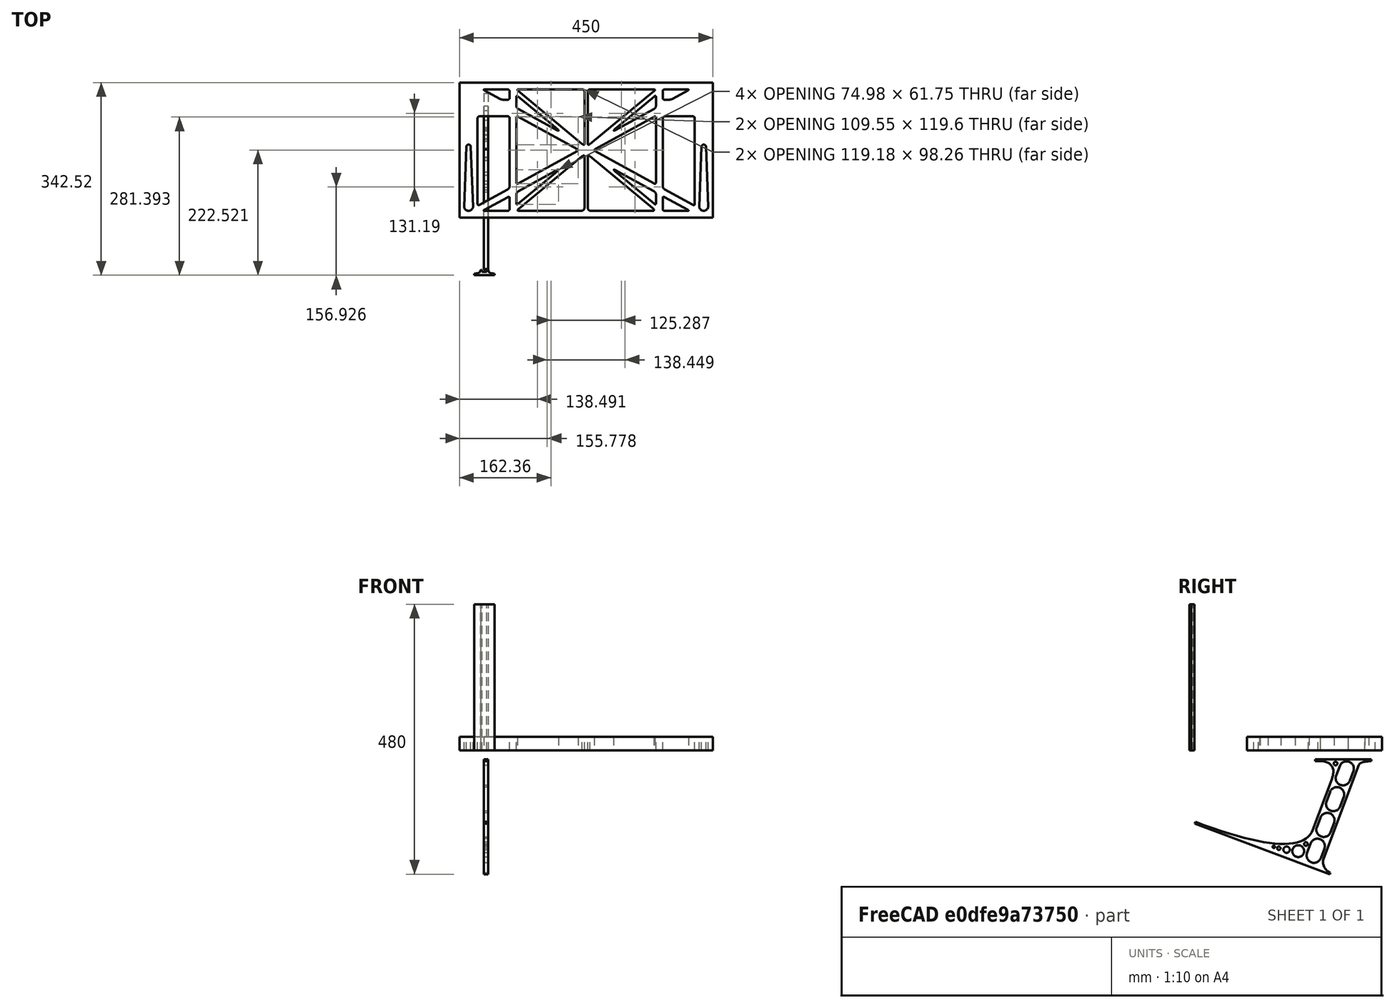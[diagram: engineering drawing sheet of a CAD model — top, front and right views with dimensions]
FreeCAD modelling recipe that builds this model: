
FCSTD DOCUMENT  (FreeCAD 0.19R0.19.2)
Label: laptopStand150FCStd
License: All rights reserved
LicenseURL: http://en.wikipedia.org/wiki/All_rights_reserved
objects: Sketcher::SketchObject×4, Part::Extrusion×3
note: 7 computed .brp shape members not serialized (recipe doc carries the construction recipe); baked Part::Feature solids carry a one-line shape summary decoded from their .brp

FEATURE [Sketcher::SketchObject] Sketch
  FullyConstrained = false
  sketch-geometry (349):
    g0: LineSegment StartX=-10.9272 StartY=-82.7794 StartZ=0 EndX=46.0728 EndY=-51.4823 EndZ=0
    g1: LineSegment StartX=-10.9272 StartY=76.4095 StartZ=0 EndX=-10.9272 EndY=-82.7794 EndZ=0
    g2: LineSegment StartX=46.0728 StartY=76.4095 StartZ=0 EndX=46.0728 EndY=-51.4823 EndZ=0
    g3: LineSegment StartX=-42.9272 StartY=136.221 StartZ=0 EndX=-42.9272 EndY=-103.779 EndZ=0
    g4: LineSegment StartX=407.073 StartY=136.221 StartZ=0 EndX=407.073 EndY=-103.779 EndZ=0
    g5: ArcOfCircle CenterX=-26.9272 CenterY=-83.7794 CenterZ=0 NormalX=0 NormalY=0 NormalZ=1 AngleXU=0 Radius=8 StartAngle=3.14159 EndAngle=6.28319
    g6: ArcOfCircle CenterX=391.073 CenterY=22.1087 CenterZ=0 NormalX=0 NormalY=0 NormalZ=1 AngleXU=0 Radius=8 StartAngle=-4.4e-15 EndAngle=3.14159
    g7: LineSegment StartX=399.073 StartY=22.1087 StartZ=0 EndX=399.073 EndY=-83.7794 EndZ=0
    g8: LineSegment StartX=383.073 StartY=22.1087 StartZ=0 EndX=383.073 EndY=-83.7794 EndZ=0
    g9: ArcOfCircle CenterX=391.073 CenterY=-83.7794 CenterZ=0 NormalX=0 NormalY=0 NormalZ=1 AngleXU=0 Radius=8 StartAngle=3.14159 EndAngle=6.28319
    g10: Circle CenterX=175.022 CenterY=27.0628 CenterZ=0 NormalX=0 NormalY=0 NormalZ=1 AngleXU=0 Radius=1
    g11: Circle CenterX=179.022 CenterY=24.8665 CenterZ=0 NormalX=0 NormalY=0 NormalZ=1 AngleXU=0 Radius=1
    g12: Circle CenterX=179.022 CenterY=27.0628 CenterZ=0 NormalX=0 NormalY=0 NormalZ=1 AngleXU=0 Radius=1
    g13: BSplineCurve PolesCount=3 KnotsCount=2 Degree=2 IsPeriodic=0
    g14: GeomPoint X=175.022 Y=27.0628 Z=0
    g15: GeomPoint X=179.022 Y=27.0628 Z=0
    g16: Circle CenterX=189.124 CenterY=27.0628 CenterZ=0 NormalX=0 NormalY=0 NormalZ=1 AngleXU=0 Radius=1
    g17: Circle CenterX=185.124 CenterY=24.8665 CenterZ=0 NormalX=0 NormalY=0 NormalZ=1 AngleXU=0 Radius=1
    g18: Circle CenterX=185.124 CenterY=27.0628 CenterZ=0 NormalX=0 NormalY=0 NormalZ=1 AngleXU=0 Radius=1
    g19: BSplineCurve PolesCount=3 KnotsCount=2 Degree=2 IsPeriodic=0
    g20: GeomPoint X=189.124 Y=27.0628 Z=0
    g21: GeomPoint X=185.124 Y=27.0628 Z=0
    g22: Circle CenterX=175.022 CenterY=5.37834 CenterZ=0 NormalX=0 NormalY=0 NormalZ=1 AngleXU=0 Radius=1
    g23: Circle CenterX=179.022 CenterY=7.57463 CenterZ=0 NormalX=0 NormalY=0 NormalZ=1 AngleXU=0 Radius=1
    g24: Circle CenterX=179.022 CenterY=5.34704 CenterZ=0 NormalX=0 NormalY=0 NormalZ=1 AngleXU=0 Radius=1
    g25: BSplineCurve PolesCount=3 KnotsCount=2 Degree=2 IsPeriodic=0
    g26: GeomPoint X=175.022 Y=5.37834 Z=0
    g27: GeomPoint X=179.022 Y=5.34704 Z=0
    g28: Circle CenterX=189.124 CenterY=5.37834 CenterZ=0 NormalX=0 NormalY=0 NormalZ=1 AngleXU=0 Radius=1
    g29: Circle CenterX=185.124 CenterY=7.57463 CenterZ=0 NormalX=0 NormalY=0 NormalZ=1 AngleXU=0 Radius=1
    g30: Circle CenterX=185.124 CenterY=5.34704 CenterZ=0 NormalX=0 NormalY=0 NormalZ=1 AngleXU=0 Radius=1
    g31: BSplineCurve PolesCount=3 KnotsCount=2 Degree=2 IsPeriodic=0
    g32: GeomPoint X=189.124 Y=5.37834 Z=0
    g33: GeomPoint X=185.124 Y=5.34704 Z=0
    g34: Circle CenterX=165.871 CenterY=18.1458 CenterZ=0 NormalX=0 NormalY=0 NormalZ=1 AngleXU=0 Radius=1
    g35: Circle CenterX=169.377 CenterY=16.2206 CenterZ=0 NormalX=0 NormalY=0 NormalZ=1 AngleXU=0 Radius=1
    g36: Circle CenterX=165.871 CenterY=14.2954 CenterZ=0 NormalX=0 NormalY=0 NormalZ=1 AngleXU=0 Radius=1
    g37: BSplineCurve PolesCount=3 KnotsCount=2 Degree=2 IsPeriodic=0
    g38: GeomPoint X=165.871 Y=18.1458 Z=0
    g39: GeomPoint X=165.871 Y=14.2954 Z=0
    g40: Circle CenterX=198.275 CenterY=18.1458 CenterZ=0 NormalX=0 NormalY=0 NormalZ=1 AngleXU=0 Radius=1
    g41: Circle CenterX=194.768 CenterY=16.2206 CenterZ=0 NormalX=0 NormalY=0 NormalZ=1 AngleXU=0 Radius=1
    g42: Circle CenterX=198.275 CenterY=14.2954 CenterZ=0 NormalX=0 NormalY=0 NormalZ=1 AngleXU=0 Radius=1
    g43: BSplineCurve PolesCount=3 KnotsCount=2 Degree=2 IsPeriodic=0
    g44: GeomPoint X=198.275 Y=18.1458 Z=0
    g45: GeomPoint X=198.275 Y=14.2954 Z=0
    g46: LineSegment StartX=407.073 StartY=-103.779 StartZ=0 EndX=-42.9272 EndY=-103.779 EndZ=0
    g47: LineSegment StartX=407.073 StartY=136.221 StartZ=0 EndX=-42.9272 EndY=136.221 EndZ=0
    g48: LineSegment StartX=46.0728 StartY=76.4095 StartZ=0 EndX=-10.9272 EndY=76.4095 EndZ=0
    g49: Circle CenterX=125.607 CenterY=54.1951 CenterZ=0 NormalX=0 NormalY=0 NormalZ=1 AngleXU=0 Radius=1
    g50: Circle CenterX=139.632 CenterY=46.4944 CenterZ=0 NormalX=0 NormalY=0 NormalZ=1 AngleXU=0 Radius=1
    g51: Circle CenterX=127.326 CenterY=56.7187 CenterZ=0 NormalX=0 NormalY=0 NormalZ=1 AngleXU=0 Radius=1
    g52: BSplineCurve PolesCount=3 KnotsCount=2 Degree=2 IsPeriodic=0
    g53: GeomPoint X=125.607 Y=54.1951 Z=0
    g54: GeomPoint X=127.326 Y=56.7187 Z=0
    g55: Circle CenterX=236.821 CenterY=56.7187 CenterZ=0 NormalX=0 NormalY=0 NormalZ=1 AngleXU=0 Radius=1
    g56: Circle CenterX=224.513 CenterY=46.4944 CenterZ=0 NormalX=0 NormalY=0 NormalZ=1 AngleXU=0 Radius=1
    g57: Circle CenterX=238.538 CenterY=54.1951 CenterZ=0 NormalX=0 NormalY=0 NormalZ=1 AngleXU=0 Radius=1
    g58: BSplineCurve PolesCount=3 KnotsCount=2 Degree=2 IsPeriodic=0
    g59: GeomPoint X=236.821 Y=56.7187 Z=0
    g60: GeomPoint X=238.538 Y=54.1951 Z=0
    g61: Circle CenterX=238.538 CenterY=-21.7539 CenterZ=0 NormalX=0 NormalY=0 NormalZ=1 AngleXU=0 Radius=1
    g62: Circle CenterX=224.513 CenterY=-14.0532 CenterZ=0 NormalX=0 NormalY=0 NormalZ=1 AngleXU=0 Radius=1
    g63: Circle CenterX=236.821 CenterY=-24.2775 CenterZ=0 NormalX=0 NormalY=0 NormalZ=1 AngleXU=0 Radius=1
    g64: BSplineCurve PolesCount=3 KnotsCount=2 Degree=2 IsPeriodic=0
    g65: GeomPoint X=238.538 Y=-21.7539 Z=0
    g66: GeomPoint X=236.821 Y=-24.2775 Z=0
    g67: Circle CenterX=125.607 CenterY=-21.7539 CenterZ=0 NormalX=0 NormalY=0 NormalZ=1 AngleXU=0 Radius=1
    g68: Circle CenterX=139.632 CenterY=-14.0532 CenterZ=0 NormalX=0 NormalY=0 NormalZ=1 AngleXU=0 Radius=1
    g69: Circle CenterX=127.325 CenterY=-24.2775 CenterZ=0 NormalX=0 NormalY=0 NormalZ=1 AngleXU=0 Radius=1
    g70: BSplineCurve PolesCount=3 KnotsCount=2 Degree=2 IsPeriodic=0
    g71: GeomPoint X=125.607 Y=-21.7539 Z=0
    g72: GeomPoint X=127.325 Y=-24.2775 Z=0
    g73: Circle CenterX=302.996 CenterY=111.695 CenterZ=0 NormalX=0 NormalY=0 NormalZ=1 AngleXU=0 Radius=1
    g74: Circle CenterX=306.073 CenterY=114.251 CenterZ=0 NormalX=0 NormalY=0 NormalZ=1 AngleXU=0 Radius=1
    g75: Circle CenterX=306.073 CenterY=110.251 CenterZ=0 NormalX=0 NormalY=0 NormalZ=1 AngleXU=0 Radius=1
    g76: BSplineCurve PolesCount=3 KnotsCount=2 Degree=2 IsPeriodic=0
    g77: GeomPoint X=302.996 Y=111.695 Z=0
    g78: GeomPoint X=306.073 Y=110.251 Z=0
    g79: Circle CenterX=306.073 CenterY=95.2763 CenterZ=0 NormalX=0 NormalY=0 NormalZ=1 AngleXU=0 Radius=1
    g80: Circle CenterX=306.073 CenterY=91.2763 CenterZ=0 NormalX=0 NormalY=0 NormalZ=1 AngleXU=0 Radius=1
    g81: Circle CenterX=302.567 CenterY=89.3511 CenterZ=0 NormalX=0 NormalY=0 NormalZ=1 AngleXU=0 Radius=1
    g82: BSplineCurve PolesCount=3 KnotsCount=2 Degree=2 IsPeriodic=0
    g83: GeomPoint X=306.073 Y=95.2763 Z=0
    g84: GeomPoint X=302.567 Y=89.3511 Z=0
    g85: LineSegment StartX=306.073 StartY=110.251 StartZ=0 EndX=306.073 EndY=95.2763 EndZ=0
    g86: LineSegment StartX=302.996 StartY=111.695 StartZ=0 EndX=236.821 EndY=56.7187 EndZ=0
    g87: LineSegment StartX=238.538 StartY=54.1951 StartZ=0 EndX=302.567 EndY=89.3511 EndZ=0
    g88: Circle CenterX=61.1496 CenterY=111.695 CenterZ=0 NormalX=0 NormalY=0 NormalZ=1 AngleXU=0 Radius=1
    g89: Circle CenterX=58.0728 CenterY=114.251 CenterZ=0 NormalX=0 NormalY=0 NormalZ=1 AngleXU=0 Radius=1
    g90: Circle CenterX=58.0728 CenterY=110.251 CenterZ=0 NormalX=0 NormalY=0 NormalZ=1 AngleXU=0 Radius=1
    g91: BSplineCurve PolesCount=3 KnotsCount=2 Degree=2 IsPeriodic=0
    g92: GeomPoint X=61.1496 Y=111.695 Z=0
    g93: GeomPoint X=58.0728 Y=110.251 Z=0
    g94: Circle CenterX=61.5791 CenterY=89.3511 CenterZ=0 NormalX=0 NormalY=0 NormalZ=1 AngleXU=0 Radius=1
    g95: Circle CenterX=58.0728 CenterY=91.2763 CenterZ=0 NormalX=0 NormalY=0 NormalZ=1 AngleXU=0 Radius=1
    g96: Circle CenterX=58.0728 CenterY=95.2763 CenterZ=0 NormalX=0 NormalY=0 NormalZ=1 AngleXU=0 Radius=1
    g97: BSplineCurve PolesCount=3 KnotsCount=2 Degree=2 IsPeriodic=0
    g98: GeomPoint X=61.5791 Y=89.3511 Z=0
    g99: GeomPoint X=58.0728 Y=95.2763 Z=0
    g100: LineSegment StartX=58.0728 StartY=110.251 StartZ=0 EndX=58.0728 EndY=95.2763 EndZ=0
    g101: LineSegment StartX=61.1496 StartY=111.695 StartZ=0 EndX=127.326 EndY=56.7187 EndZ=0
    g102: LineSegment StartX=125.607 StartY=54.1951 StartZ=0 EndX=61.5791 EndY=89.3511 EndZ=0
    g103: Circle CenterX=61.5791 CenterY=-56.9099 CenterZ=0 NormalX=0 NormalY=0 NormalZ=1 AngleXU=0 Radius=1
    g104: Circle CenterX=58.0728 CenterY=-58.8351 CenterZ=0 NormalX=0 NormalY=0 NormalZ=1 AngleXU=0 Radius=1
    g105: Circle CenterX=58.0728 CenterY=-62.8351 CenterZ=0 NormalX=0 NormalY=0 NormalZ=1 AngleXU=0 Radius=1
    g106: BSplineCurve PolesCount=3 KnotsCount=2 Degree=2 IsPeriodic=0
    g107: GeomPoint X=61.5791 Y=-56.9099 Z=0
    g108: GeomPoint X=58.0728 Y=-62.8351 Z=0
    g109: Circle CenterX=58.0728 CenterY=-77.8102 CenterZ=0 NormalX=0 NormalY=0 NormalZ=1 AngleXU=0 Radius=1
    g110: Circle CenterX=58.0728 CenterY=-81.8102 CenterZ=0 NormalX=0 NormalY=0 NormalZ=1 AngleXU=0 Radius=1
    g111: Circle CenterX=61.1496 CenterY=-79.2541 CenterZ=0 NormalX=0 NormalY=0 NormalZ=1 AngleXU=0 Radius=1
    g112: BSplineCurve PolesCount=3 KnotsCount=2 Degree=2 IsPeriodic=0
    g113: GeomPoint X=58.0728 Y=-77.8102 Z=0
    g114: GeomPoint X=61.1496 Y=-79.2541 Z=0
    g115: LineSegment StartX=58.0728 StartY=-62.8351 StartZ=0 EndX=58.0728 EndY=-77.8102 EndZ=0
    g116: LineSegment StartX=61.1496 StartY=-79.2541 StartZ=0 EndX=127.325 EndY=-24.2775 EndZ=0
    g117: LineSegment StartX=125.607 StartY=-21.7539 StartZ=0 EndX=61.5791 EndY=-56.9099 EndZ=0
    g118: Circle CenterX=302.567 CenterY=-56.9099 CenterZ=0 NormalX=0 NormalY=0 NormalZ=1 AngleXU=0 Radius=1
    g119: Circle CenterX=306.073 CenterY=-58.8351 CenterZ=0 NormalX=0 NormalY=0 NormalZ=1 AngleXU=0 Radius=1
    g120: Circle CenterX=306.073 CenterY=-62.8351 CenterZ=0 NormalX=0 NormalY=0 NormalZ=1 AngleXU=0 Radius=1
    g121: BSplineCurve PolesCount=3 KnotsCount=2 Degree=2 IsPeriodic=0
    g122: GeomPoint X=302.567 Y=-56.9099 Z=0
    g123: GeomPoint X=306.073 Y=-62.8351 Z=0
    g124: Circle CenterX=302.996 CenterY=-79.2541 CenterZ=0 NormalX=0 NormalY=0 NormalZ=1 AngleXU=0 Radius=1
    g125: Circle CenterX=306.073 CenterY=-81.8102 CenterZ=0 NormalX=0 NormalY=0 NormalZ=1 AngleXU=0 Radius=1
    g126: Circle CenterX=306.073 CenterY=-77.8102 CenterZ=0 NormalX=0 NormalY=0 NormalZ=1 AngleXU=0 Radius=1
    g127: BSplineCurve PolesCount=3 KnotsCount=2 Degree=2 IsPeriodic=0
    g128: GeomPoint X=302.996 Y=-79.2541 Z=0
    g129: GeomPoint X=306.073 Y=-77.8102 Z=0
    g130: LineSegment StartX=306.073 StartY=-62.8351 StartZ=0 EndX=306.073 EndY=-77.8102 EndZ=0
    g131: LineSegment StartX=302.996 StartY=-79.2541 StartZ=0 EndX=236.821 EndY=-24.2775 EndZ=0
    g132: LineSegment StartX=238.538 StartY=-21.7539 StartZ=0 EndX=302.567 EndY=-56.9099 EndZ=0
    g133: Circle CenterX=61.6457 CenterY=-88.8112 CenterZ=0 NormalX=0 NormalY=0 NormalZ=1 AngleXU=0 Radius=1
    g134: Circle CenterX=58.0728 CenterY=-91.7794 CenterZ=0 NormalX=0 NormalY=0 NormalZ=1 AngleXU=0 Radius=1
    g135: Circle CenterX=63.9135 CenterY=-91.7794 CenterZ=0 NormalX=0 NormalY=0 NormalZ=1 AngleXU=0 Radius=1
    g136: BSplineCurve PolesCount=3 KnotsCount=2 Degree=2 IsPeriodic=0
    g137: GeomPoint X=61.6457 Y=-88.8112 Z=0
    g138: GeomPoint X=63.9135 Y=-91.7794 Z=0
    g139: Circle CenterX=179.022 CenterY=-85.8163 CenterZ=0 NormalX=0 NormalY=0 NormalZ=1 AngleXU=0 Radius=1
    g140: Circle CenterX=179.022 CenterY=-91.7794 CenterZ=0 NormalX=0 NormalY=0 NormalZ=1 AngleXU=0 Radius=1
    g141: Circle CenterX=171.895 CenterY=-91.7794 CenterZ=0 NormalX=0 NormalY=0 NormalZ=1 AngleXU=0 Radius=1
    g142: BSplineCurve PolesCount=3 KnotsCount=2 Degree=2 IsPeriodic=0
    g143: GeomPoint X=179.022 Y=-85.8163 Z=0
    g144: GeomPoint X=171.895 Y=-91.7794 Z=0
    g145: Circle CenterX=185.124 CenterY=-86.2028 CenterZ=0 NormalX=0 NormalY=0 NormalZ=1 AngleXU=0 Radius=1
    g146: Circle CenterX=185.124 CenterY=-91.7794 CenterZ=0 NormalX=0 NormalY=0 NormalZ=1 AngleXU=0 Radius=1
    g147: Circle CenterX=191.747 CenterY=-91.7794 CenterZ=0 NormalX=0 NormalY=0 NormalZ=1 AngleXU=0 Radius=1
    g148: BSplineCurve PolesCount=3 KnotsCount=2 Degree=2 IsPeriodic=0
    g149: GeomPoint X=185.124 Y=-86.2028 Z=0
    g150: GeomPoint X=191.747 Y=-91.7794 Z=0
    g151: Circle CenterX=299.888 CenterY=-86.6413 CenterZ=0 NormalX=0 NormalY=0 NormalZ=1 AngleXU=0 Radius=1
    g152: Circle CenterX=306.073 CenterY=-91.7794 CenterZ=0 NormalX=0 NormalY=0 NormalZ=1 AngleXU=0 Radius=1
    g153: Circle CenterX=298.776 CenterY=-91.7794 CenterZ=0 NormalX=0 NormalY=0 NormalZ=1 AngleXU=0 Radius=1
    g154: BSplineCurve PolesCount=3 KnotsCount=2 Degree=2 IsPeriodic=0
    g155: GeomPoint X=299.888 Y=-86.6413 Z=0
    g156: GeomPoint X=298.776 Y=-91.7794 Z=0
    g157: LineSegment StartX=189.124 StartY=5.37834 StartZ=0 EndX=299.888 EndY=-86.6413 EndZ=0
    g158: LineSegment StartX=298.776 StartY=-91.7794 StartZ=0 EndX=191.747 EndY=-91.7794 EndZ=0
    g159: LineSegment StartX=185.124 StartY=-86.2028 StartZ=0 EndX=185.124 EndY=5.34704 EndZ=0
    g160: LineSegment StartX=179.022 StartY=5.34704 StartZ=0 EndX=179.022 EndY=-85.8163 EndZ=0
    g161: LineSegment StartX=171.895 StartY=-91.7794 StartZ=0 EndX=63.9135 EndY=-91.7794 EndZ=0
    g162: LineSegment StartX=61.6457 StartY=-88.8112 StartZ=0 EndX=175.022 EndY=5.37834 EndZ=0
    g163: Circle CenterX=302.073 CenterY=124.221 CenterZ=0 NormalX=0 NormalY=0 NormalZ=1 AngleXU=0 Radius=1
    g164: Circle CenterX=306.073 CenterY=124.221 CenterZ=0 NormalX=0 NormalY=0 NormalZ=1 AngleXU=0 Radius=1
    g165: Circle CenterX=302.996 CenterY=121.665 CenterZ=0 NormalX=0 NormalY=0 NormalZ=1 AngleXU=0 Radius=1
    g166: BSplineCurve PolesCount=3 KnotsCount=2 Degree=2 IsPeriodic=0
    g167: GeomPoint X=302.073 Y=124.221 Z=0
    g168: GeomPoint X=302.996 Y=121.665 Z=0
    g169: Circle CenterX=189.124 CenterY=124.221 CenterZ=0 NormalX=0 NormalY=0 NormalZ=1 AngleXU=0 Radius=1
    g170: Circle CenterX=185.124 CenterY=124.221 CenterZ=0 NormalX=0 NormalY=0 NormalZ=1 AngleXU=0 Radius=1
    g171: Circle CenterX=185.124 CenterY=120.221 CenterZ=0 NormalX=0 NormalY=0 NormalZ=1 AngleXU=0 Radius=1
    g172: BSplineCurve PolesCount=3 KnotsCount=2 Degree=2 IsPeriodic=0
    g173: GeomPoint X=189.124 Y=124.221 Z=0
    g174: GeomPoint X=185.124 Y=120.221 Z=0
    g175: Circle CenterX=175.022 CenterY=124.221 CenterZ=0 NormalX=0 NormalY=0 NormalZ=1 AngleXU=0 Radius=1
    g176: Circle CenterX=179.022 CenterY=124.221 CenterZ=0 NormalX=0 NormalY=0 NormalZ=1 AngleXU=0 Radius=1
    g177: Circle CenterX=179.022 CenterY=120.221 CenterZ=0 NormalX=0 NormalY=0 NormalZ=1 AngleXU=0 Radius=1
    g178: BSplineCurve PolesCount=3 KnotsCount=2 Degree=2 IsPeriodic=0
    g179: GeomPoint X=175.022 Y=124.221 Z=0
    g180: GeomPoint X=179.022 Y=120.221 Z=0
    g181: Circle CenterX=62.0728 CenterY=124.221 CenterZ=0 NormalX=0 NormalY=0 NormalZ=1 AngleXU=0 Radius=1
    g182: Circle CenterX=58.0728 CenterY=124.221 CenterZ=0 NormalX=0 NormalY=0 NormalZ=1 AngleXU=0 Radius=1
    g183: Circle CenterX=61.1496 CenterY=121.665 CenterZ=0 NormalX=0 NormalY=0 NormalZ=1 AngleXU=0 Radius=1
    g184: BSplineCurve PolesCount=3 KnotsCount=2 Degree=2 IsPeriodic=0
    g185: GeomPoint X=62.0728 Y=124.221 Z=0
    g186: GeomPoint X=61.1496 Y=121.665 Z=0
    g187: LineSegment StartX=62.0728 StartY=124.221 StartZ=0 EndX=175.022 EndY=124.221 EndZ=0
    g188: LineSegment StartX=179.022 StartY=120.221 StartZ=0 EndX=179.022 EndY=27.0628 EndZ=0
    g189: LineSegment StartX=185.124 StartY=27.0628 StartZ=0 EndX=185.124 EndY=120.221 EndZ=0
    g190: LineSegment StartX=189.124 StartY=124.221 StartZ=0 EndX=302.073 EndY=124.221 EndZ=0
    g191: LineSegment StartX=302.996 StartY=121.665 StartZ=0 EndX=189.124 EndY=27.0628 EndZ=0
    g192: LineSegment StartX=175.022 StartY=27.0628 StartZ=0 EndX=61.1496 EndY=121.665 EndZ=0
    g193: Circle CenterX=61.5791 CenterY=75.4095 CenterZ=0 NormalX=0 NormalY=0 NormalZ=1 AngleXU=0 Radius=1
    g194: Circle CenterX=58.0728 CenterY=77.3346 CenterZ=0 NormalX=0 NormalY=0 NormalZ=1 AngleXU=0 Radius=1
    g195: Circle CenterX=58.0728 CenterY=73.3346 CenterZ=0 NormalX=0 NormalY=0 NormalZ=1 AngleXU=0 Radius=1
    g196: BSplineCurve PolesCount=3 KnotsCount=2 Degree=2 IsPeriodic=0
    g197: GeomPoint X=61.5791 Y=75.4095 Z=0
    g198: GeomPoint X=58.0728 Y=73.3346 Z=0
    g199: Circle CenterX=58.0728 CenterY=-40.8935 CenterZ=0 NormalX=0 NormalY=0 NormalZ=1 AngleXU=0 Radius=1
    g200: Circle CenterX=58.0728 CenterY=-44.8935 CenterZ=0 NormalX=0 NormalY=0 NormalZ=1 AngleXU=0 Radius=1
    g201: Circle CenterX=61.5791 CenterY=-42.9683 CenterZ=0 NormalX=0 NormalY=0 NormalZ=1 AngleXU=0 Radius=1
    g202: BSplineCurve PolesCount=3 KnotsCount=2 Degree=2 IsPeriodic=0
    g203: GeomPoint X=58.0728 Y=-40.8935 Z=0
    g204: GeomPoint X=61.5791 Y=-42.9683 Z=0
    g205: LineSegment StartX=61.5791 StartY=-42.9683 StartZ=0 EndX=165.871 EndY=14.2954 EndZ=0
    g206: LineSegment StartX=165.871 StartY=18.1458 StartZ=0 EndX=61.5791 EndY=75.4095 EndZ=0
    g207: LineSegment StartX=58.0728 StartY=73.3346 StartZ=0 EndX=58.0728 EndY=-40.8935 EndZ=0
    g208: Circle CenterX=302.567 CenterY=-42.9683 CenterZ=0 NormalX=0 NormalY=0 NormalZ=1 AngleXU=0 Radius=1
    g209: Circle CenterX=306.073 CenterY=-44.8935 CenterZ=0 NormalX=0 NormalY=0 NormalZ=1 AngleXU=0 Radius=1
    g210: Circle CenterX=306.073 CenterY=-40.8935 CenterZ=0 NormalX=0 NormalY=0 NormalZ=1 AngleXU=0 Radius=1
    g211: BSplineCurve PolesCount=3 KnotsCount=2 Degree=2 IsPeriodic=0
    g212: GeomPoint X=302.567 Y=-42.9683 Z=0
    g213: GeomPoint X=306.073 Y=-40.8935 Z=0
    g214: Circle CenterX=306.073 CenterY=73.3346 CenterZ=0 NormalX=0 NormalY=0 NormalZ=1 AngleXU=0 Radius=1
    g215: Circle CenterX=306.073 CenterY=77.3346 CenterZ=0 NormalX=0 NormalY=0 NormalZ=1 AngleXU=0 Radius=1
    g216: Circle CenterX=302.567 CenterY=75.4095 CenterZ=0 NormalX=0 NormalY=0 NormalZ=1 AngleXU=0 Radius=1
    g217: BSplineCurve PolesCount=3 KnotsCount=2 Degree=2 IsPeriodic=0
    g218: GeomPoint X=306.073 Y=73.3346 Z=0
    g219: GeomPoint X=302.567 Y=75.4095 Z=0
    g220: LineSegment StartX=302.567 StartY=-42.9683 StartZ=0 EndX=198.275 EndY=14.2954 EndZ=0
    g221: LineSegment StartX=198.275 StartY=18.1458 StartZ=0 EndX=302.567 EndY=75.4095 EndZ=0
    g222: LineSegment StartX=306.073 StartY=73.3346 StartZ=0 EndX=306.073 EndY=-40.8935 EndZ=0
    g223: LineSegment StartX=322.073 StartY=105.865 StartZ=0 EndX=328.643 EndY=105.865 EndZ=0
    g224: LineSegment StartX=318.073 StartY=120.221 StartZ=0 EndX=318.073 EndY=109.865 EndZ=0
    g225: LineSegment StartX=336.157 StartY=107.779 StartZ=0 EndX=362.567 EndY=122.294 EndZ=0
    g226: Circle CenterX=362.073 CenterY=124.221 CenterZ=0 NormalX=0 NormalY=0 NormalZ=1 AngleXU=0 Radius=1
    g227: Circle CenterX=366.073 CenterY=124.221 CenterZ=0 NormalX=0 NormalY=0 NormalZ=1 AngleXU=0 Radius=1
    g228: Circle CenterX=362.567 CenterY=122.294 CenterZ=0 NormalX=0 NormalY=0 NormalZ=1 AngleXU=0 Radius=1
    g229: BSplineCurve PolesCount=3 KnotsCount=2 Degree=2 IsPeriodic=0
    g230: GeomPoint X=362.073 Y=124.221 Z=0
    g231: GeomPoint X=362.567 Y=122.294 Z=0
    g232: Circle CenterX=322.073 CenterY=124.221 CenterZ=0 NormalX=0 NormalY=0 NormalZ=1 AngleXU=0 Radius=1
    g233: Circle CenterX=318.073 CenterY=124.221 CenterZ=0 NormalX=0 NormalY=0 NormalZ=1 AngleXU=0 Radius=1
    g234: Circle CenterX=318.073 CenterY=120.221 CenterZ=0 NormalX=0 NormalY=0 NormalZ=1 AngleXU=0 Radius=1
    g235: BSplineCurve PolesCount=3 KnotsCount=2 Degree=2 IsPeriodic=0
    g236: GeomPoint X=322.073 Y=124.221 Z=0
    g237: GeomPoint X=318.073 Y=120.221 Z=0
    g238: Circle CenterX=322.073 CenterY=105.865 CenterZ=0 NormalX=0 NormalY=0 NormalZ=1 AngleXU=0 Radius=1
    g239: Circle CenterX=318.073 CenterY=105.865 CenterZ=0 NormalX=0 NormalY=0 NormalZ=1 AngleXU=0 Radius=1
    g240: Circle CenterX=318.073 CenterY=109.865 CenterZ=0 NormalX=0 NormalY=0 NormalZ=1 AngleXU=0 Radius=1
    g241: BSplineCurve PolesCount=3 KnotsCount=2 Degree=2 IsPeriodic=0
    g242: GeomPoint X=322.073 Y=105.865 Z=0
    g243: GeomPoint X=318.073 Y=109.865 Z=0
    g244: Circle CenterX=336.157 CenterY=107.779 CenterZ=0 NormalX=0 NormalY=0 NormalZ=1 AngleXU=0 Radius=1
    g245: Circle CenterX=332.651 CenterY=105.853 CenterZ=0 NormalX=0 NormalY=0 NormalZ=1 AngleXU=0 Radius=1
    g246: Circle CenterX=328.643 CenterY=105.865 CenterZ=0 NormalX=0 NormalY=0 NormalZ=1 AngleXU=0 Radius=1
    g247: BSplineCurve PolesCount=3 KnotsCount=2 Degree=2 IsPeriodic=0
    g248: GeomPoint X=336.157 Y=107.779 Z=0
    g249: GeomPoint X=328.643 Y=105.865 Z=0
    g250: LineSegment StartX=322.073 StartY=124.221 StartZ=0 EndX=362.073 EndY=124.221 EndZ=0
    g251: Circle CenterX=371.567 CenterY=-80.8644 CenterZ=0 NormalX=0 NormalY=0 NormalZ=1 AngleXU=0 Radius=1
    g252: Circle CenterX=375.073 CenterY=-82.7896 CenterZ=0 NormalX=0 NormalY=0 NormalZ=1 AngleXU=0 Radius=1
    g253: Circle CenterX=375.073 CenterY=-78.7896 CenterZ=0 NormalX=0 NormalY=0 NormalZ=1 AngleXU=0 Radius=1
    g254: BSplineCurve PolesCount=3 KnotsCount=2 Degree=2 IsPeriodic=0
    g255: GeomPoint X=371.567 Y=-80.8644 Z=0
    g256: GeomPoint X=375.073 Y=-78.7896 Z=0
    g257: Circle CenterX=321.579 CenterY=-53.4075 CenterZ=0 NormalX=0 NormalY=0 NormalZ=1 AngleXU=0 Radius=1
    g258: Circle CenterX=318.073 CenterY=-51.4823 CenterZ=0 NormalX=0 NormalY=0 NormalZ=1 AngleXU=0 Radius=1
    g259: Circle CenterX=318.073 CenterY=-47.4805 CenterZ=0 NormalX=0 NormalY=0 NormalZ=1 AngleXU=0 Radius=1
    g260: BSplineCurve PolesCount=3 KnotsCount=2 Degree=2 IsPeriodic=0
    g261: GeomPoint X=321.579 Y=-53.4075 Z=0
    g262: GeomPoint X=318.073 Y=-47.4805 Z=0
    g263: LineSegment StartX=371.567 StartY=-80.8644 StartZ=0 EndX=321.579 EndY=-53.4075 EndZ=0
    g264: Circle CenterX=321.579 CenterY=-67.3492 CenterZ=0 NormalX=0 NormalY=0 NormalZ=1 AngleXU=0 Radius=1
    g265: Circle CenterX=318.073 CenterY=-65.424 CenterZ=0 NormalX=0 NormalY=0 NormalZ=1 AngleXU=0 Radius=1
    g266: Circle CenterX=318.073 CenterY=-69.424 CenterZ=0 NormalX=0 NormalY=0 NormalZ=1 AngleXU=0 Radius=1
    g267: BSplineCurve PolesCount=3 KnotsCount=2 Degree=2 IsPeriodic=0
    g268: GeomPoint X=321.579 Y=-67.3492 Z=0
    g269: GeomPoint X=318.073 Y=-69.424 Z=0
    g270: Circle CenterX=362.567 CenterY=-89.8542 CenterZ=0 NormalX=0 NormalY=0 NormalZ=1 AngleXU=0 Radius=1
    g271: Circle CenterX=366.073 CenterY=-91.7794 CenterZ=0 NormalX=0 NormalY=0 NormalZ=1 AngleXU=0 Radius=1
    g272: Circle CenterX=362.073 CenterY=-91.7794 CenterZ=0 NormalX=0 NormalY=0 NormalZ=1 AngleXU=0 Radius=1
    g273: BSplineCurve PolesCount=3 KnotsCount=2 Degree=2 IsPeriodic=0
    g274: GeomPoint X=362.567 Y=-89.8542 Z=0
    g275: GeomPoint X=362.073 Y=-91.7794 Z=0
    g276: Circle CenterX=322.073 CenterY=-91.7794 CenterZ=0 NormalX=0 NormalY=0 NormalZ=1 AngleXU=0 Radius=1
    g277: Circle CenterX=318.073 CenterY=-91.7794 CenterZ=0 NormalX=0 NormalY=0 NormalZ=1 AngleXU=0 Radius=1
    g278: Circle CenterX=318.073 CenterY=-87.7794 CenterZ=0 NormalX=0 NormalY=0 NormalZ=1 AngleXU=0 Radius=1
    g279: BSplineCurve PolesCount=3 KnotsCount=2 Degree=2 IsPeriodic=0
    g280: GeomPoint X=322.073 Y=-91.7794 Z=0
    g281: GeomPoint X=318.073 Y=-87.7794 Z=0
    g282: LineSegment StartX=362.567 StartY=-89.8542 StartZ=0 EndX=321.579 EndY=-67.3492 EndZ=0
    g283: LineSegment StartX=318.073 StartY=-69.424 StartZ=0 EndX=318.073 EndY=-87.7794 EndZ=0
    g284: LineSegment StartX=322.073 StartY=-91.7794 StartZ=0 EndX=362.073 EndY=-91.7794 EndZ=0
    g285: Circle CenterX=2.07281 CenterY=124.221 CenterZ=0 NormalX=0 NormalY=0 NormalZ=1 AngleXU=0 Radius=1
    g286: Circle CenterX=1.57905 CenterY=122.295 CenterZ=0 NormalX=0 NormalY=0 NormalZ=1 AngleXU=0 Radius=1
    g287: BSplineCurve PolesCount=3 KnotsCount=2 Degree=2 IsPeriodic=0
    g288: GeomPoint X=2.07281 Y=124.221 Z=0
    g289: GeomPoint X=1.57905 Y=122.295 Z=0
    g290: Circle CenterX=42.0728 CenterY=124.221 CenterZ=0 NormalX=0 NormalY=0 NormalZ=1 AngleXU=0 Radius=1
    g291: Circle CenterX=46.0728 CenterY=124.221 CenterZ=0 NormalX=0 NormalY=0 NormalZ=1 AngleXU=0 Radius=1
    g292: Circle CenterX=46.0728 CenterY=120.221 CenterZ=0 NormalX=0 NormalY=0 NormalZ=1 AngleXU=0 Radius=1
    g293: BSplineCurve PolesCount=3 KnotsCount=2 Degree=2 IsPeriodic=0
    g294: GeomPoint X=42.0728 Y=124.221 Z=0
    g295: GeomPoint X=46.0728 Y=120.221 Z=0
    g296: Circle CenterX=46.0728 CenterY=109.865 CenterZ=0 NormalX=0 NormalY=0 NormalZ=1 AngleXU=0 Radius=1
    g297: Circle CenterX=46.0728 CenterY=105.865 CenterZ=0 NormalX=0 NormalY=0 NormalZ=1 AngleXU=0 Radius=1
    g298: Circle CenterX=42.0728 CenterY=105.865 CenterZ=0 NormalX=0 NormalY=0 NormalZ=1 AngleXU=0 Radius=1
    g299: BSplineCurve PolesCount=3 KnotsCount=2 Degree=2 IsPeriodic=0
    g300: GeomPoint X=46.0728 Y=109.865 Z=0
    g301: GeomPoint X=42.0728 Y=105.865 Z=0
    g302: Circle CenterX=35.5028 CenterY=105.865 CenterZ=0 NormalX=0 NormalY=0 NormalZ=1 AngleXU=0 Radius=1
    g303: Circle CenterX=31.5028 CenterY=105.865 CenterZ=0 NormalX=0 NormalY=0 NormalZ=1 AngleXU=0 Radius=1
    g304: Circle CenterX=27.9965 CenterY=107.79 CenterZ=0 NormalX=0 NormalY=0 NormalZ=1 AngleXU=0 Radius=1
    g305: BSplineCurve PolesCount=3 KnotsCount=2 Degree=2 IsPeriodic=0
    g306: GeomPoint X=35.5028 Y=105.865 Z=0
    g307: GeomPoint X=27.9965 Y=107.79 Z=0
    g308: LineSegment StartX=2.07281 StartY=124.221 StartZ=0 EndX=42.0728 EndY=124.221 EndZ=0
    g309: LineSegment StartX=46.0728 StartY=120.221 StartZ=0 EndX=46.0728 EndY=109.865 EndZ=0
    g310: LineSegment StartX=42.0728 StartY=105.865 StartZ=0 EndX=35.5028 EndY=105.865 EndZ=0
    g311: LineSegment StartX=27.9965 StartY=107.79 StartZ=0 EndX=1.57905 EndY=122.295 EndZ=0
    g312: Circle CenterX=42.5666 CenterY=-67.3492 CenterZ=0 NormalX=0 NormalY=0 NormalZ=1 AngleXU=0 Radius=1
    g313: Circle CenterX=46.0728 CenterY=-65.424 CenterZ=0 NormalX=0 NormalY=0 NormalZ=1 AngleXU=0 Radius=1
    g314: Circle CenterX=46.0728 CenterY=-69.424 CenterZ=0 NormalX=0 NormalY=0 NormalZ=1 AngleXU=0 Radius=1
    g315: BSplineCurve PolesCount=3 KnotsCount=2 Degree=2 IsPeriodic=0
    g316: GeomPoint X=42.5666 Y=-67.3492 Z=0
    g317: GeomPoint X=46.0728 Y=-69.424 Z=0
    g318: Circle CenterX=46.0728 CenterY=-87.7794 CenterZ=0 NormalX=0 NormalY=0 NormalZ=1 AngleXU=0 Radius=1
    g319: Circle CenterX=46.0728 CenterY=-91.7794 CenterZ=0 NormalX=0 NormalY=0 NormalZ=1 AngleXU=0 Radius=1
    g320: Circle CenterX=42.0728 CenterY=-91.7794 CenterZ=0 NormalX=0 NormalY=0 NormalZ=1 AngleXU=0 Radius=1
    g321: BSplineCurve PolesCount=3 KnotsCount=2 Degree=2 IsPeriodic=0
    g322: GeomPoint X=46.0728 Y=-87.7794 Z=0
    g323: GeomPoint X=42.0728 Y=-91.7794 Z=0
    g324: Circle CenterX=2.07281 CenterY=-91.7794 CenterZ=0 NormalX=0 NormalY=0 NormalZ=1 AngleXU=0 Radius=1
    g325: Circle CenterX=-1.92719 CenterY=-91.7794 CenterZ=0 NormalX=0 NormalY=0 NormalZ=1 AngleXU=0 Radius=1
    g326: Circle CenterX=1.57905 CenterY=-89.8542 CenterZ=0 NormalX=0 NormalY=0 NormalZ=1 AngleXU=0 Radius=1
    g327: BSplineCurve PolesCount=3 KnotsCount=2 Degree=2 IsPeriodic=0
    g328: GeomPoint X=2.07281 Y=-91.7794 Z=0
    g329: GeomPoint X=1.57905 Y=-89.8542 Z=0
    g330: LineSegment StartX=2.07281 StartY=-91.7794 StartZ=0 EndX=42.0728 EndY=-91.7794 EndZ=0
    g331: LineSegment StartX=46.0728 StartY=-87.7794 StartZ=0 EndX=46.0728 EndY=-69.424 EndZ=0
    g332: LineSegment StartX=42.5666 StartY=-67.3492 StartZ=0 EndX=1.57905 EndY=-89.8542 EndZ=0
    g333: Circle CenterX=322.073 CenterY=76.4095 CenterZ=0 NormalX=0 NormalY=0 NormalZ=1 AngleXU=0 Radius=4
    g334: BSplineCurve PolesCount=3 KnotsCount=2 Degree=2 IsPeriodic=0
    g335: GeomPoint X=318.073 Y=72.4095 Z=0
    g336: GeomPoint X=322.073 Y=76.4095 Z=0
    g337: Circle CenterX=375.073 CenterY=72.4095 CenterZ=0 NormalX=0 NormalY=0 NormalZ=1 AngleXU=0 Radius=1
    g338: Circle CenterX=375.073 CenterY=76.4095 CenterZ=0 NormalX=0 NormalY=0 NormalZ=1 AngleXU=0 Radius=1
    g339: Circle CenterX=371.073 CenterY=76.4095 CenterZ=0 NormalX=0 NormalY=0 NormalZ=1 AngleXU=0 Radius=1
    g340: BSplineCurve PolesCount=3 KnotsCount=2 Degree=2 IsPeriodic=0
    g341: GeomPoint X=375.073 Y=72.4095 Z=0
    g342: GeomPoint X=371.073 Y=76.4095 Z=0
    g343: LineSegment StartX=322.073 StartY=76.4095 StartZ=0 EndX=371.073 EndY=76.4095 EndZ=0
    g344: LineSegment StartX=318.073 StartY=72.4095 StartZ=0 EndX=318.073 EndY=-47.4805 EndZ=0
    g345: LineSegment StartX=375.073 StartY=72.4095 StartZ=0 EndX=375.073 EndY=-78.7896 EndZ=0
    g346: ArcOfCircle CenterX=-26.9272 CenterY=22.1087 CenterZ=0 NormalX=0 NormalY=0 NormalZ=1 AngleXU=0 Radius=4 StartAngle=5e-16 EndAngle=3.14159
    g347: LineSegment StartX=-30.9272 StartY=22.1087 StartZ=0 EndX=-34.9272 EndY=-83.7794 EndZ=0
    g348: LineSegment StartX=-18.9272 StartY=-83.7794 StartZ=0 EndX=-22.9272 EndY=22.1087 EndZ=0
  constraints (572):
    c: Coincident(g0,g2)
    c: Block(g0)
    c: Block(g1)
    c: Vertical(g3)
    c: Vertical(g4)
    c: Block(g4)
    c: Block(g3)
    c: Tangent(g6,g7) = 1.5708
    c: Tangent(g7,g9) = 1.5708
    c: Equal(g6,g9)
    c: Coincident(g8,g6)
    c: Coincident(g8,g9)
    c: Block(g7)
    c: Block(g8)
    c: Weight(g10) = 1
    c: Equal(g10,g11)
    c: Equal(g10,g12)
    c: InternalAlignment(g10,g13)
    c: InternalAlignment(g11,g13)
    c: InternalAlignment(g12,g13)
    c: InternalAlignment(g14,g13)
    c: InternalAlignment(g15,g13)
    c: Weight(g16) = 1
    c: Equal(g16,g17)
    c: Equal(g16,g18)
    c: InternalAlignment(g16,g19)
    c: InternalAlignment(g17,g19)
    c: InternalAlignment(g18,g19)
    c: InternalAlignment(g20,g19)
    c: InternalAlignment(g21,g19)
    c: Block(g19)
    c: Block(g13)
    c: Weight(g22) = 1
    c: Equal(g22,g23)
    c: Equal(g22,g24)
    c: InternalAlignment(g22,g25)
    c: InternalAlignment(g23,g25)
    c: InternalAlignment(g24,g25)
    c: InternalAlignment(g26,g25)
    c: InternalAlignment(g27,g25)
    c: Weight(g28) = 1
    c: Equal(g28,g29)
    c: Equal(g28,g30)
    c: InternalAlignment(g28,g31)
    c: InternalAlignment(g29,g31)
    c: InternalAlignment(g30,g31)
    c: InternalAlignment(g32,g31)
    c: InternalAlignment(g33,g31)
    c: Block(g31)
    c: Block(g25)
    c: Weight(g34) = 1
    c: Equal(g34,g35)
    c: Equal(g34,g36)
    c: InternalAlignment(g34,g37)
    c: InternalAlignment(g35,g37)
    c: InternalAlignment(g36,g37)
    c: InternalAlignment(g38,g37)
    c: InternalAlignment(g39,g37)
    c: Weight(g40) = 1
    c: Equal(g40,g41)
    c: Equal(g40,g42)
    c: InternalAlignment(g40,g43)
    c: InternalAlignment(g41,g43)
    c: InternalAlignment(g42,g43)
    c: InternalAlignment(g44,g43)
    c: InternalAlignment(g45,g43)
    c: Block(g37)
    c: Block(g43)
    c: Coincident(g46,g4)
    c: Coincident(g46,g3)
    c: Horizontal(g46)
    c: Distance(g46) = 450
    c: Coincident(g47,g4)
    c: Coincident(g47,g3)
    c: Horizontal(g47)
    c: Horizontal(g48)
    c: Coincident(g2,g48)
    c: Block(g48)
    c: Coincident(g1,g48)
    c: Weight(g49) = 1
    c: Equal(g49,g50)
    c: Equal(g49,g51)
    c: InternalAlignment(g49,g52)
    c: InternalAlignment(g50,g52)
    c: InternalAlignment(g51,g52)
    c: InternalAlignment(g53,g52)
    c: InternalAlignment(g54,g52)
    c: Block(g52)
    c: Weight(g55) = 1
    c: Equal(g55,g56)
    c: Equal(g55,g57)
    c: InternalAlignment(g55,g58)
    c: InternalAlignment(g56,g58)
    c: InternalAlignment(g57,g58)
    c: InternalAlignment(g59,g58)
    c: InternalAlignment(g60,g58)
    c: Block(g58)
    c: Weight(g61) = 1
    c: Equal(g61,g62)
    c: Equal(g61,g63)
    c: InternalAlignment(g61,g64)
    c: InternalAlignment(g62,g64)
    c: InternalAlignment(g63,g64)
    c: InternalAlignment(g65,g64)
    c: InternalAlignment(g66,g64)
    c: Block(g64)
    c: Weight(g67) = 1
    c: Equal(g67,g68)
    c: Equal(g67,g69)
    c: InternalAlignment(g67,g70)
    c: InternalAlignment(g68,g70)
    c: InternalAlignment(g69,g70)
    c: InternalAlignment(g71,g70)
    c: InternalAlignment(g72,g70)
    c: Block(g70)
    c: Weight(g73) = 1
    c: Equal(g73,g74)
    c: Equal(g73,g75)
    c: InternalAlignment(g73,g76)
    c: InternalAlignment(g74,g76)
    c: InternalAlignment(g75,g76)
    c: InternalAlignment(g77,g76)
    c: InternalAlignment(g78,g76)
    c: Weight(g79) = 1
    c: Equal(g79,g80)
    c: Equal(g79,g81)
    c: InternalAlignment(g79,g82)
    c: InternalAlignment(g80,g82)
    c: InternalAlignment(g81,g82)
    c: InternalAlignment(g83,g82)
    c: InternalAlignment(g84,g82)
    c: Block(g76)
    c: Block(g82)
    c: Coincident(g85,g76)
    c: Coincident(g85,g82)
    c: Vertical(g85)
    c: Coincident(g86,g76)
    c: Coincident(g86,g58)
    c: Coincident(g87,g58)
    c: Coincident(g87,g82)
    c: Weight(g88) = 1
    c: Equal(g88,g89)
    c: Equal(g88,g90)
    c: InternalAlignment(g88,g91)
    c: InternalAlignment(g89,g91)
    c: InternalAlignment(g90,g91)
    c: InternalAlignment(g92,g91)
    c: InternalAlignment(g93,g91)
    c: Weight(g94) = 1
    c: Equal(g94,g95)
    c: Equal(g94,g96)
    c: InternalAlignment(g94,g97)
    c: InternalAlignment(g95,g97)
    c: InternalAlignment(g96,g97)
    c: InternalAlignment(g98,g97)
    c: InternalAlignment(g99,g97)
    c: Block(g91)
    c: Block(g97)
    c: Coincident(g100,g91)
    c: Coincident(g100,g97)
    c: Vertical(g100)
    c: Coincident(g101,g91)
    c: Coincident(g101,g52)
    c: Coincident(g102,g52)
    c: Coincident(g102,g97)
    c: Weight(g103) = 1
    c: Equal(g103,g104)
    c: Equal(g103,g105)
    c: InternalAlignment(g103,g106)
    c: InternalAlignment(g104,g106)
    c: InternalAlignment(g105,g106)
    c: InternalAlignment(g107,g106)
    c: InternalAlignment(g108,g106)
    c: Weight(g109) = 1
    c: Equal(g109,g110)
    c: Equal(g109,g111)
    c: InternalAlignment(g109,g112)
    c: InternalAlignment(g110,g112)
    c: InternalAlignment(g111,g112)
    c: InternalAlignment(g113,g112)
    c: InternalAlignment(g114,g112)
    c: Block(g106)
    c: Block(g112)
    c: Coincident(g115,g106)
    c: Coincident(g115,g112)
    c: Vertical(g115)
    c: Coincident(g116,g112)
    c: Coincident(g116,g70)
    c: Coincident(g117,g70)
    c: Coincident(g117,g106)
    c: Weight(g118) = 1
    c: Equal(g118,g119)
    c: Equal(g118,g120)
    c: InternalAlignment(g118,g121)
    c: InternalAlignment(g119,g121)
    c: InternalAlignment(g120,g121)
    c: InternalAlignment(g122,g121)
    c: InternalAlignment(g123,g121)
    c: Weight(g124) = 1
    c: Equal(g124,g125)
    c: Equal(g124,g126)
    c: InternalAlignment(g124,g127)
    c: InternalAlignment(g125,g127)
    c: InternalAlignment(g126,g127)
    c: InternalAlignment(g128,g127)
    c: InternalAlignment(g129,g127)
    c: Block(g121)
    c: Block(g127)
    c: Coincident(g130,g121)
    c: Coincident(g130,g127)
    c: Vertical(g130)
    c: Coincident(g131,g127)
    c: Coincident(g131,g64)
    c: Coincident(g132,g64)
    c: Coincident(g132,g121)
    c: Weight(g133) = 1
    c: Equal(g133,g134)
    c: Equal(g133,g135)
    c: InternalAlignment(g133,g136)
    c: InternalAlignment(g134,g136)
    c: InternalAlignment(g135,g136)
    c: InternalAlignment(g137,g136)
    c: InternalAlignment(g138,g136)
    c: Weight(g139) = 1
    c: Equal(g139,g140)
    c: Equal(g139,g141)
    c: InternalAlignment(g139,g142)
    c: InternalAlignment(g140,g142)
    c: InternalAlignment(g141,g142)
    c: InternalAlignment(g143,g142)
    c: InternalAlignment(g144,g142)
    c: Weight(g145) = 1
    c: Equal(g145,g146)
    c: Equal(g145,g147)
    c: InternalAlignment(g145,g148)
    c: InternalAlignment(g146,g148)
    c: InternalAlignment(g147,g148)
    c: InternalAlignment(g149,g148)
    c: InternalAlignment(g150,g148)
    c: Weight(g151) = 1
    c: Equal(g151,g152)
    c: Equal(g151,g153)
    c: InternalAlignment(g151,g154)
    c: InternalAlignment(g152,g154)
    c: InternalAlignment(g153,g154)
    c: InternalAlignment(g155,g154)
    c: InternalAlignment(g156,g154)
    c: Block(g154)
    c: Block(g148)
    c: Block(g142)
    c: Block(g136)
    c: Coincident(g157,g31)
    c: Coincident(g157,g154)
    c: Coincident(g158,g154)
    c: Coincident(g158,g148)
    c: Horizontal(g158)
    c: Coincident(g159,g148)
    c: Coincident(g159,g31)
    c: Vertical(g159)
    c: Coincident(g160,g25)
    c: Coincident(g160,g142)
    c: Vertical(g160)
    c: Coincident(g161,g142)
    c: Coincident(g161,g136)
    c: Horizontal(g161)
    c: Coincident(g162,g136)
    c: Coincident(g162,g25)
    c: Weight(g163) = 1
    c: Equal(g163,g164)
    c: Equal(g163,g165)
    c: InternalAlignment(g163,g166)
    c: InternalAlignment(g164,g166)
    c: InternalAlignment(g165,g166)
    c: InternalAlignment(g167,g166)
    c: InternalAlignment(g168,g166)
    c: Weight(g169) = 1
    c: Equal(g169,g170)
    c: Equal(g169,g171)
    c: InternalAlignment(g169,g172)
    c: InternalAlignment(g170,g172)
    c: InternalAlignment(g171,g172)
    c: InternalAlignment(g173,g172)
    c: InternalAlignment(g174,g172)
    c: Weight(g175) = 1
    c: Equal(g175,g176)
    c: Equal(g175,g177)
    c: InternalAlignment(g175,g178)
    c: InternalAlignment(g176,g178)
    c: InternalAlignment(g177,g178)
    c: InternalAlignment(g179,g178)
    c: InternalAlignment(g180,g178)
    c: Weight(g181) = 1
    c: Equal(g181,g182)
    c: Equal(g181,g183)
    c: InternalAlignment(g181,g184)
    c: InternalAlignment(g182,g184)
    c: InternalAlignment(g183,g184)
    c: InternalAlignment(g185,g184)
    c: InternalAlignment(g186,g184)
    c: Block(g184)
    c: Block(g178)
    c: Block(g172)
    c: Block(g166)
    c: Coincident(g187,g184)
    c: Coincident(g187,g178)
    c: Horizontal(g187)
    c: Coincident(g188,g178)
    c: Coincident(g188,g13)
    c: Vertical(g188)
    c: Coincident(g189,g19)
    c: Coincident(g189,g172)
    c: Vertical(g189)
    c: Coincident(g190,g172)
    c: Coincident(g190,g166)
    c: Horizontal(g190)
    c: Coincident(g191,g166)
    c: Coincident(g191,g19)
    c: Coincident(g192,g13)
    c: Weight(g193) = 1
    c: Equal(g193,g194)
    c: Equal(g193,g195)
    c: InternalAlignment(g193,g196)
    c: InternalAlignment(g194,g196)
    c: InternalAlignment(g195,g196)
    c: InternalAlignment(g197,g196)
    c: InternalAlignment(g198,g196)
    c: Weight(g199) = 1
    c: Equal(g199,g200)
    c: Equal(g199,g201)
    c: InternalAlignment(g199,g202)
    c: InternalAlignment(g200,g202)
    c: InternalAlignment(g201,g202)
    c: InternalAlignment(g203,g202)
    c: InternalAlignment(g204,g202)
    c: Block(g202)
    c: Block(g196)
    c: Coincident(g205,g202)
    c: Coincident(g205,g37)
    c: Coincident(g206,g37)
    c: Coincident(g206,g196)
    c: Coincident(g207,g196)
    c: Coincident(g207,g202)
    c: Vertical(g207)
    c: Weight(g208) = 1
    c: Equal(g208,g209)
    c: Equal(g208,g210)
    c: InternalAlignment(g208,g211)
    c: InternalAlignment(g209,g211)
    c: InternalAlignment(g210,g211)
    c: InternalAlignment(g212,g211)
    c: InternalAlignment(g213,g211)
    c: Weight(g214) = 1
    c: Equal(g214,g215)
    c: Equal(g214,g216)
    c: InternalAlignment(g214,g217)
    c: InternalAlignment(g215,g217)
    c: InternalAlignment(g216,g217)
    c: InternalAlignment(g218,g217)
    c: InternalAlignment(g219,g217)
    c: Block(g217)
    c: Block(g211)
    c: Coincident(g220,g211)
    c: Coincident(g220,g43)
    c: Coincident(g221,g43)
    c: Coincident(g221,g217)
    c: Coincident(g222,g217)
    c: Coincident(g222,g211)
    c: Vertical(g222)
    c: Horizontal(g223)
    c: Block(g223)
    c: Vertical(g224)
    c: Block(g224)
    c: Block(g225)
    c: Weight(g226) = 1
    c: Equal(g226,g227)
    c: Equal(g226,g228)
    c: InternalAlignment(g226,g229)
    c: InternalAlignment(g227,g229)
    c: InternalAlignment(g228,g229)
    c: InternalAlignment(g230,g229)
    c: InternalAlignment(g231,g229)
    c: Weight(g232) = 1
    c: Equal(g232,g233)
    c: Equal(g232,g234)
    c: InternalAlignment(g232,g235)
    c: InternalAlignment(g233,g235)
    c: InternalAlignment(g234,g235)
    c: InternalAlignment(g236,g235)
    c: InternalAlignment(g237,g235)
    c: Weight(g238) = 1
    c: Equal(g238,g239)
    c: Equal(g238,g240)
    c: InternalAlignment(g238,g241)
    c: InternalAlignment(g239,g241)
    c: InternalAlignment(g240,g241)
    c: InternalAlignment(g242,g241)
    c: InternalAlignment(g243,g241)
    c: Weight(g244) = 1
    c: Equal(g244,g245)
    c: Equal(g244,g246)
    c: InternalAlignment(g244,g247)
    c: InternalAlignment(g245,g247)
    c: InternalAlignment(g246,g247)
    c: InternalAlignment(g248,g247)
    c: InternalAlignment(g249,g247)
    c: Block(g229)
    c: Block(g235)
    c: Block(g241)
    c: Block(g247)
    c: Coincident(g250,g235)
    c: Coincident(g250,g229)
    c: Horizontal(g250)
    c: Block(g192)
    c: Weight(g251) = 1
    c: Equal(g251,g252)
    c: Equal(g251,g253)
    c: InternalAlignment(g251,g254)
    c: InternalAlignment(g252,g254)
    c: InternalAlignment(g253,g254)
    c: InternalAlignment(g255,g254)
    c: InternalAlignment(g256,g254)
    c: Weight(g257) = 1
    c: Equal(g257,g258)
    c: Equal(g257,g259)
    c: InternalAlignment(g257,g260)
    c: InternalAlignment(g258,g260)
    c: InternalAlignment(g259,g260)
    c: InternalAlignment(g261,g260)
    c: InternalAlignment(g262,g260)
    c: Block(g254)
    c: Block(g260)
    c: Coincident(g263,g254)
    c: Coincident(g263,g260)
    c: Weight(g264) = 1
    c: Equal(g264,g265)
    c: Equal(g264,g266)
    c: InternalAlignment(g264,g267)
    c: InternalAlignment(g265,g267)
    c: InternalAlignment(g266,g267)
    c: InternalAlignment(g268,g267)
    c: InternalAlignment(g269,g267)
    c: Weight(g270) = 1
    c: Equal(g270,g271)
    c: Equal(g270,g272)
    c: InternalAlignment(g270,g273)
    c: InternalAlignment(g271,g273)
    c: InternalAlignment(g272,g273)
    c: InternalAlignment(g274,g273)
    c: InternalAlignment(g275,g273)
    c: Weight(g276) = 1
    c: Equal(g276,g277)
    c: Equal(g276,g278)
    c: InternalAlignment(g276,g279)
    c: InternalAlignment(g277,g279)
    c: InternalAlignment(g278,g279)
    c: InternalAlignment(g280,g279)
    c: InternalAlignment(g281,g279)
    c: Block(g279)
    c: Block(g273)
    c: Block(g267)
    c: Coincident(g282,g273)
    c: Coincident(g282,g267)
    c: Coincident(g283,g267)
    c: Coincident(g283,g279)
    c: Vertical(g283)
    c: Coincident(g284,g279)
    c: Coincident(g284,g273)
    c: Horizontal(g284)
    c: Weight(g285) = 1
    c: Equal(g285,g286)
    c: InternalAlignment(g285,g287)
    c: InternalAlignment(g286,g287)
    c: InternalAlignment(g288,g287)
    c: InternalAlignment(g289,g287)
    c: Weight(g290) = 1
    c: InternalAlignment(g291,g293)
    c: InternalAlignment(g292,g293)
    c: InternalAlignment(g294,g293)
    c: InternalAlignment(g295,g293)
    c: Weight(g296) = 1
    c: Equal(g296,g297)
    c: Equal(g296,g298)
    c: InternalAlignment(g296,g299)
    c: InternalAlignment(g297,g299)
    c: InternalAlignment(g298,g299)
    c: InternalAlignment(g300,g299)
    c: InternalAlignment(g301,g299)
    c: Equal(g302,g303)
    c: Equal(g302,g304)
    c: InternalAlignment(g302,g305)
    c: InternalAlignment(g303,g305)
    c: InternalAlignment(g304,g305)
    c: InternalAlignment(g306,g305)
    c: InternalAlignment(g307,g305)
    c: Block(g293)
    c: Block(g299)
    c: Block(g305)
    c: Block(g287)
    c: Coincident(g308,g287)
    c: Coincident(g308,g293)
    c: Horizontal(g308)
    c: Coincident(g309,g293)
    c: Coincident(g309,g299)
    c: Vertical(g309)
    c: Coincident(g310,g299)
    c: Coincident(g310,g305)
    c: Horizontal(g310)
    c: Coincident(g311,g305)
    c: Coincident(g311,g287)
    c: Weight(g312) = 1
    c: Equal(g312,g313)
    c: Equal(g312,g314)
    c: InternalAlignment(g312,g315)
    c: InternalAlignment(g313,g315)
    c: InternalAlignment(g314,g315)
    c: InternalAlignment(g316,g315)
    c: InternalAlignment(g317,g315)
    c: Weight(g318) = 1
    c: Equal(g318,g319)
    c: Equal(g318,g320)
    c: InternalAlignment(g318,g321)
    c: InternalAlignment(g319,g321)
    c: InternalAlignment(g320,g321)
    c: InternalAlignment(g322,g321)
    c: InternalAlignment(g323,g321)
    c: Weight(g324) = 1
    c: Equal(g324,g325)
    c: Equal(g324,g326)
    c: InternalAlignment(g324,g327)
    c: InternalAlignment(g325,g327)
    c: InternalAlignment(g326,g327)
    c: InternalAlignment(g328,g327)
    c: InternalAlignment(g329,g327)
    c: Block(g327)
    c: Block(g321)
    c: Block(g315)
    c: Coincident(g330,g327)
    c: Coincident(g330,g321)
    c: Horizontal(g330)
    c: Coincident(g331,g321)
    c: Coincident(g331,g315)
    c: Vertical(g331)
    c: Coincident(g332,g315)
    c: Coincident(g332,g327)
    c: InternalAlignment(g333,g334)
    c: InternalAlignment(g335,g334)
    c: InternalAlignment(g336,g334)
    c: Block(g334)
    c: Equal(g337,g338)
    c: Equal(g337,g339)
    c: InternalAlignment(g337,g340)
    c: InternalAlignment(g338,g340)
    c: InternalAlignment(g339,g340)
    c: InternalAlignment(g341,g340)
    c: InternalAlignment(g342,g340)
    c: Block(g340)
    c: Coincident(g343,g334)
    c: Horizontal(g343)
    c: Block(g343)
    c: Coincident(g344,g334)
    c: Coincident(g344,g260)
    c: Vertical(g344)
    c: Coincident(g345,g340)
    c: Coincident(g345,g254)
    c: Vertical(g345)
    c: Coincident(g347,g5)
    c: Coincident(g348,g5)
    c: Block(g346)
    c: Block(g5)
    c: Block(g348)
    c: Block(g347)
    c: Distance(g344) = 119.89
FEATURE [Sketcher::SketchObject] Sketch001
  FullyConstrained = true
  MapMode = 4
  Placement = pos=(0,0,0) rot=(0.57735,0.57735,0.57735;2.0944rad)
  Support = -> [Sketch]
  sketch-geometry (46):
    g0: BSplineCurve PolesCount=3 KnotsCount=2 Degree=2 IsPeriodic=0
    g1: ArcOfCircle CenterX=73.1223 CenterY=-32.291 CenterZ=0 NormalX=0 NormalY=0 NormalZ=1 AngleXU=0 Radius=13 StartAngle=5.92268 EndAngle=9.06428
    g2: ArcOfCircle CenterX=66.7816 CenterY=-49.1439 CenterZ=0 NormalX=0 NormalY=0 NormalZ=1 AngleXU=0 Radius=13 StartAngle=2.78068 EndAngle=5.92131
    g3: ArcOfCircle CenterX=55.9263 CenterY=-78.1807 CenterZ=0 NormalX=0 NormalY=0 NormalZ=1 AngleXU=0 Radius=13 StartAngle=5.92268 EndAngle=9.06428
    g4: ArcOfCircle CenterX=49.5884 CenterY=-95.0342 CenterZ=0 NormalX=0 NormalY=0 NormalZ=1 AngleXU=0 Radius=13 StartAngle=2.78068 EndAngle=5.92131
    g5: ArcOfCircle CenterX=38.7206 CenterY=-124.067 CenterZ=0 NormalX=0 NormalY=0 NormalZ=1 AngleXU=0 Radius=13 StartAngle=5.92268 EndAngle=9.06428
    g6: ArcOfCircle CenterX=32.3875 CenterY=-140.92 CenterZ=0 NormalX=0 NormalY=0 NormalZ=1 AngleXU=0 Radius=13 StartAngle=2.78068 EndAngle=5.92131
    g7: ArcOfCircle CenterX=21.4715 CenterY=-169.934 CenterZ=0 NormalX=0 NormalY=0 NormalZ=1 AngleXU=0 Radius=13 StartAngle=5.92268 EndAngle=9.06428
    g8: ArcOfCircle CenterX=15.1336 CenterY=-186.787 CenterZ=0 NormalX=0 NormalY=0 NormalZ=1 AngleXU=0 Radius=13 StartAngle=2.78068 EndAngle=5.92131
    g9-g12: Circle x4 (B-spline internal-alignment scaffolding for g13; pole/knot coordinates omitted)
    g13: BSplineCurve PolesCount=4 KnotsCount=2 Degree=3 IsPeriodic=0
    g14: GeomPoint X=28.8094 Y=-19.0875 Z=0
    g15: GeomPoint X=47.0443 Y=-50.4712 Z=0
    g16: Circle CenterX=53.5586 CenterY=-23.2695 CenterZ=0 NormalX=0 NormalY=0 NormalZ=1 AngleXU=0 Radius=3.24518
    g17: Circle CenterX=-195.441 CenterY=-127.082 CenterZ=0 NormalX=0 NormalY=0 NormalZ=1 AngleXU=0 Radius=1
    g18: Circle CenterX=-8.24091 CenterY=-197.481 CenterZ=0 NormalX=0 NormalY=0 NormalZ=1 AngleXU=0 Radius=1
    g19: Circle CenterX=12.8789 CenterY=-141.321 CenterZ=0 NormalX=0 NormalY=0 NormalZ=1 AngleXU=0 Radius=1
    g20: BSplineCurve PolesCount=3 KnotsCount=2 Degree=2 IsPeriodic=0
    g21: GeomPoint X=-195.441 Y=-127.082 Z=0
    g22: GeomPoint X=12.8789 Y=-141.321 Z=0
    g23: Circle CenterX=-12.8016 CenterY=-179.036 CenterZ=0 NormalX=0 NormalY=0 NormalZ=1 AngleXU=0 Radius=10.5072
    g24: Circle CenterX=0.933922 CenterY=-166.43 CenterZ=0 NormalX=0 NormalY=0 NormalZ=1 AngleXU=0 Radius=3.26661
    g25: Circle CenterX=-33.5518 CenterY=-176.44 CenterZ=0 NormalX=0 NormalY=0 NormalZ=1 AngleXU=0 Radius=5.64388
    g26: Circle CenterX=-47.2366 CenterY=-173.859 CenterZ=0 NormalX=0 NormalY=0 NormalZ=1 AngleXU=0 Radius=3.01653
    g27: Circle CenterX=-56.2595 CenterY=-171.456 CenterZ=0 NormalX=0 NormalY=0 NormalZ=1 AngleXU=0 Radius=2.12826
    g28: ArcOfCircle CenterX=51.2151 CenterY=-198.473 CenterZ=0 NormalX=0 NormalY=0 NormalZ=1 AngleXU=0 Radius=20 StartAngle=2.78189 EndAngle=4.35269
    g29: LineSegment StartX=32.4951 StartY=-191.433 StartZ=0 EndX=94.6578 EndY=-26.1352 EndZ=0
    g30: LineSegment StartX=43.1192 StartY=-220.001 StartZ=0 EndX=-196.497 EndY=-129.89 EndZ=0
    g31: LineSegment StartX=43.1192 StartY=-220.001 StartZ=0 EndX=44.1752 EndY=-217.193 EndZ=0
    g32: LineSegment StartX=117.223 StartY=-19.0875 StartZ=0 EndX=117.223 EndY=-16.0875 EndZ=0
    g33: LineSegment StartX=117.223 StartY=-16.0875 StartZ=0 EndX=17.2232 EndY=-16.0875 EndZ=0
    g34: LineSegment StartX=17.2232 StartY=-16.0875 StartZ=0 EndX=17.2232 EndY=-19.0875 EndZ=0
    g35: LineSegment StartX=28.8094 StartY=-19.0875 StartZ=0 EndX=17.2232 EndY=-19.0875 EndZ=0
    g36: LineSegment StartX=47.0443 StartY=-50.4712 StartZ=0 EndX=12.8789 EndY=-141.321 EndZ=0
    g37: LineSegment StartX=-195.441 StartY=-127.082 StartZ=0 EndX=-196.497 EndY=-129.89 EndZ=0
    g38: LineSegment StartX=85.2866 StartY=-36.8766 StartZ=0 EndX=78.9396 EndY=-53.7463 EndZ=0
    g39: LineSegment StartX=60.9579 StartY=-27.7053 StartZ=0 EndX=54.6191 EndY=-44.5532 EndZ=0
    g40: LineSegment StartX=68.0907 StartY=-82.7664 StartZ=0 EndX=61.7465 EndY=-99.6365 EndZ=0
    g41: LineSegment StartX=43.7619 StartY=-73.595 StartZ=0 EndX=37.426 EndY=-90.4435 EndZ=0
    g42: LineSegment StartX=50.885 StartY=-128.652 StartZ=0 EndX=44.5456 EndY=-145.522 EndZ=0
    g43: LineSegment StartX=26.5562 StartY=-119.481 StartZ=0 EndX=20.2251 EndY=-136.329 EndZ=0
    g44: LineSegment StartX=9.3071 StartY=-165.349 StartZ=0 EndX=2.97115 EndY=-182.197 EndZ=0
    g45: LineSegment StartX=33.6358 StartY=-174.52 StartZ=0 EndX=27.2917 EndY=-191.39 EndZ=0
  constraints (71):
    c: Block(g0)
    c: Block(g1)
    c: Block(g2)
    c: Block(g4)
    c: Block(g3)
    c: Block(g6)
    c: Block(g5)
    c: Block(g8)
    c: Block(g7)
    c: Weight(g9) = 1
    c: Equal(g9,g10)
    c: Equal(g9,g11)
    c: Equal(g9,g12)
    c: InternalAlignment(g9-g12 -> g13) x4
    c: InternalAlignment(g14,g13)
    c: InternalAlignment(g15,g13)
    c: Block(g16)
    c: Weight(g17) = 1
    c: Equal(g17,g18)
    c: Equal(g17,g19)
    c: InternalAlignment(g17,g20)
    c: InternalAlignment(g18,g20)
    c: InternalAlignment(g19,g20)
    c: InternalAlignment(g21,g20)
    c: InternalAlignment(g22,g20)
    c: Block(g20)
    c: Block(g23)
    c: Block(g24)
    c: Block(g25)
    c: Block(g26)
    c: Block(g27)
    c: Block(g28)
    c: Coincident(g29,g28)
    c: Coincident(g29,g0)
    c: Block(g13)
    c: Coincident(g31,g30)
    c: Coincident(g31,g28)
    c: Block(g31)
    c: Coincident(g32,g0)
    c: Vertical(g32)
    c: Coincident(g33,g32)
    c: Horizontal(g33)
    c: Coincident(g34,g33)
    c: Vertical(g34)
    c: Block(g33)
    c: Coincident(g35,g13)
    c: Coincident(g35,g34)
    c: Horizontal(g35)
    c: Coincident(g36,g13)
    c: Coincident(g36,g20)
    c: Coincident(g37,g20)
    c: Coincident(g37,g30)
    c: Block(g30)
    c: Coincident(g38,g1)
    c: Coincident(g38,g2)
    c: Coincident(g39,g1)
    c: Coincident(g39,g2)
    c: Coincident(g40,g3)
    c: Coincident(g40,g4)
    c: Coincident(g41,g3)
    c: Coincident(g41,g4)
    c: Coincident(g42,g5)
    c: Coincident(g42,g6)
    c: Coincident(g43,g5)
    c: Coincident(g43,g6)
    c: Coincident(g44,g7)
    c: Coincident(g44,g8)
    c: Coincident(g45,g7)
    c: Coincident(g45,g8)
    c: Distance(g30) = 256
    c: Distance(g33) = 100
FEATURE [Part::Extrusion] Extrude002
  Base = -> Sketch001
  Dir = (1,0,0)
  DirMode = 2
  FaceMakerClass = Part::FaceMakerBullseye
  LengthFwd = 8
  LengthRev = 0
  Solid = true
  Symmetric = false
FEATURE [Sketcher::SketchObject] Sketch002
  FullyConstrained = true
  sketch-geometry (20):
    g0: LineSegment StartX=-2.77179 StartY=-200.304 StartZ=0 EndX=5.22821 EndY=-200.304 EndZ=0
    g1: LineSegment StartX=5.22821 StartY=-200.304 StartZ=0 EndX=5.22821 EndY=-197.304 EndZ=0
    g2: LineSegment StartX=-2.77179 StartY=-200.304 StartZ=0 EndX=-2.77179 EndY=-197.304 EndZ=0
    g3: LineSegment StartX=5.22821 StartY=-197.304 StartZ=0 EndX=8.22821 EndY=-197.304 EndZ=0
    g4: LineSegment StartX=-2.77179 StartY=-197.304 StartZ=0 EndX=-5.77179 EndY=-197.304 EndZ=0
    g5: LineSegment StartX=19.2282 StartY=-203.304 StartZ=0 EndX=19.2282 EndY=-206.304 EndZ=0
    g6: LineSegment StartX=-16.7718 StartY=-203.304 StartZ=0 EndX=-16.7718 EndY=-206.304 EndZ=0
    g7: LineSegment StartX=-16.7718 StartY=-206.304 StartZ=0 EndX=19.2282 EndY=-206.304 EndZ=0
    g8: Circle CenterX=-16.7718 CenterY=-203.304 CenterZ=0 NormalX=0 NormalY=0 NormalZ=1 AngleXU=0 Radius=1
    g9: Circle CenterX=-5.77179 CenterY=-203.304 CenterZ=0 NormalX=0 NormalY=0 NormalZ=1 AngleXU=0 Radius=1
    g10: Circle CenterX=-5.77179 CenterY=-197.304 CenterZ=0 NormalX=0 NormalY=0 NormalZ=1 AngleXU=0 Radius=1
    g11: BSplineCurve PolesCount=3 KnotsCount=2 Degree=2 IsPeriodic=0
    g12: GeomPoint X=-16.7718 Y=-203.304 Z=0
    g13: GeomPoint X=-5.77179 Y=-197.304 Z=0
    g14: Circle CenterX=19.2282 CenterY=-203.304 CenterZ=0 NormalX=0 NormalY=0 NormalZ=1 AngleXU=0 Radius=1
    g15: Circle CenterX=8.22821 CenterY=-203.304 CenterZ=0 NormalX=0 NormalY=0 NormalZ=1 AngleXU=0 Radius=1
    g16: Circle CenterX=8.22821 CenterY=-197.304 CenterZ=0 NormalX=0 NormalY=0 NormalZ=1 AngleXU=0 Radius=1
    g17: BSplineCurve PolesCount=3 KnotsCount=2 Degree=2 IsPeriodic=0
    g18: GeomPoint X=19.2282 Y=-203.304 Z=0
    g19: GeomPoint X=8.22821 Y=-197.304 Z=0
  constraints (41):
    c: Horizontal(g0)
    c: Distance(g0) = 8
    c: Coincident(g1,g0)
    c: Vertical(g1)
    c: Distance(g1) = 3
    c: Coincident(g2,g0)
    c: Vertical(g2)
    c: Distance(g2) = 3
    c: Coincident(g3,g1)
    c: Horizontal(g3)
    c: Distance(g3) = 3
    c: Coincident(g4,g2)
    c: Horizontal(g4)
    c: Distance(g4) = 3
    c: Vertical(g5)
    c: Vertical(g6)
    c: Coincident(g7,g6)
    c: Coincident(g7,g5)
    c: Weight(g8) = 1
    c: Equal(g8,g9)
    c: Equal(g8,g10)
    c: Coincident(g11,g4)
    c: InternalAlignment(g8,g11)
    c: InternalAlignment(g9,g11)
    c: InternalAlignment(g10,g11)
    c: InternalAlignment(g12,g11)
    c: InternalAlignment(g13,g11)
    c: Coincident(g17,g5)
    c: Weight(g14) = 1
    c: Equal(g14,g15)
    c: Equal(g14,g16)
    c: Coincident(g17,g3)
    c: InternalAlignment(g14,g17)
    c: InternalAlignment(g15,g17)
    c: InternalAlignment(g16,g17)
    c: InternalAlignment(g18,g17)
    c: InternalAlignment(g19,g17)
    c: Block(g7)
    c: Block(g17)
    c: Block(g11)
    c: Block(g6)
FEATURE [Part::Extrusion] Extrude003
  Base = -> Sketch002
  Dir = (0,0,1)
  DirMode = 2
  FaceMakerClass = Part::FaceMakerBullseye
  LengthFwd = 260
  LengthRev = 0
  Solid = true
  Symmetric = false
FEATURE [Sketcher::SketchObject] Sketch003
  FullyConstrained = false
  sketch-geometry (373):
    g0: LineSegment StartX=-42.9272 StartY=136.221 StartZ=0 EndX=-42.9272 EndY=-103.779 EndZ=0
    g1: LineSegment StartX=407.073 StartY=136.221 StartZ=0 EndX=407.073 EndY=-103.779 EndZ=0
    g2: ArcOfCircle CenterX=-26.9272 CenterY=-83.7794 CenterZ=0 NormalX=0 NormalY=0 NormalZ=1 AngleXU=0 Radius=8 StartAngle=3.14159 EndAngle=6.28319
    g3: ArcOfCircle CenterX=391.073 CenterY=-83.7794 CenterZ=0 NormalX=0 NormalY=0 NormalZ=1 AngleXU=0 Radius=8 StartAngle=3.14159 EndAngle=6.28319
    g4: Circle CenterX=175.022 CenterY=27.0628 CenterZ=0 NormalX=0 NormalY=0 NormalZ=1 AngleXU=0 Radius=1
    g5: Circle CenterX=179.022 CenterY=24.8665 CenterZ=0 NormalX=0 NormalY=0 NormalZ=1 AngleXU=0 Radius=1
    g6: Circle CenterX=179.022 CenterY=27.0628 CenterZ=0 NormalX=0 NormalY=0 NormalZ=1 AngleXU=0 Radius=1
    g7: BSplineCurve PolesCount=3 KnotsCount=2 Degree=2 IsPeriodic=0
    g8: GeomPoint X=175.022 Y=27.0628 Z=0
    g9: GeomPoint X=179.022 Y=27.0628 Z=0
    g10: Circle CenterX=189.124 CenterY=27.0628 CenterZ=0 NormalX=0 NormalY=0 NormalZ=1 AngleXU=0 Radius=1
    g11: Circle CenterX=185.124 CenterY=24.8665 CenterZ=0 NormalX=0 NormalY=0 NormalZ=1 AngleXU=0 Radius=1
    g12: Circle CenterX=185.124 CenterY=27.0628 CenterZ=0 NormalX=0 NormalY=0 NormalZ=1 AngleXU=0 Radius=1
    g13: BSplineCurve PolesCount=3 KnotsCount=2 Degree=2 IsPeriodic=0
    g14: GeomPoint X=189.124 Y=27.0628 Z=0
    g15: GeomPoint X=185.124 Y=27.0628 Z=0
    g16: Circle CenterX=175.022 CenterY=5.37834 CenterZ=0 NormalX=0 NormalY=0 NormalZ=1 AngleXU=0 Radius=1
    g17: Circle CenterX=179.022 CenterY=7.57463 CenterZ=0 NormalX=0 NormalY=0 NormalZ=1 AngleXU=0 Radius=1
    g18: Circle CenterX=179.022 CenterY=5.34704 CenterZ=0 NormalX=0 NormalY=0 NormalZ=1 AngleXU=0 Radius=1
    g19: BSplineCurve PolesCount=3 KnotsCount=2 Degree=2 IsPeriodic=0
    g20: GeomPoint X=175.022 Y=5.37834 Z=0
    g21: GeomPoint X=179.022 Y=5.34704 Z=0
    g22: Circle CenterX=189.124 CenterY=5.37834 CenterZ=0 NormalX=0 NormalY=0 NormalZ=1 AngleXU=0 Radius=1
    g23: Circle CenterX=185.124 CenterY=7.57463 CenterZ=0 NormalX=0 NormalY=0 NormalZ=1 AngleXU=0 Radius=1
    g24: Circle CenterX=185.124 CenterY=5.34704 CenterZ=0 NormalX=0 NormalY=0 NormalZ=1 AngleXU=0 Radius=1
    g25: BSplineCurve PolesCount=3 KnotsCount=2 Degree=2 IsPeriodic=0
    g26: GeomPoint X=189.124 Y=5.37834 Z=0
    g27: GeomPoint X=185.124 Y=5.34704 Z=0
    g28: Circle CenterX=165.871 CenterY=18.1458 CenterZ=0 NormalX=0 NormalY=0 NormalZ=1 AngleXU=0 Radius=1
    g29: Circle CenterX=169.377 CenterY=16.2206 CenterZ=0 NormalX=0 NormalY=0 NormalZ=1 AngleXU=0 Radius=1
    g30: Circle CenterX=165.871 CenterY=14.2954 CenterZ=0 NormalX=0 NormalY=0 NormalZ=1 AngleXU=0 Radius=1
    g31: BSplineCurve PolesCount=3 KnotsCount=2 Degree=2 IsPeriodic=0
    g32: GeomPoint X=165.871 Y=18.1458 Z=0
    g33: GeomPoint X=165.871 Y=14.2954 Z=0
    g34: Circle CenterX=198.275 CenterY=18.1458 CenterZ=0 NormalX=0 NormalY=0 NormalZ=1 AngleXU=0 Radius=1
    g35: Circle CenterX=194.768 CenterY=16.2206 CenterZ=0 NormalX=0 NormalY=0 NormalZ=1 AngleXU=0 Radius=1
    g36: Circle CenterX=198.275 CenterY=14.2954 CenterZ=0 NormalX=0 NormalY=0 NormalZ=1 AngleXU=0 Radius=1
    g37: BSplineCurve PolesCount=3 KnotsCount=2 Degree=2 IsPeriodic=0
    g38: GeomPoint X=198.275 Y=18.1458 Z=0
    g39: GeomPoint X=198.275 Y=14.2954 Z=0
    g40: LineSegment StartX=407.073 StartY=-103.779 StartZ=0 EndX=-42.9272 EndY=-103.779 EndZ=0
    g41: LineSegment StartX=407.073 StartY=136.221 StartZ=0 EndX=-42.9272 EndY=136.221 EndZ=0
    g42: Circle CenterX=125.607 CenterY=54.1951 CenterZ=0 NormalX=0 NormalY=0 NormalZ=1 AngleXU=0 Radius=1
    g43: Circle CenterX=139.632 CenterY=46.4944 CenterZ=0 NormalX=0 NormalY=0 NormalZ=1 AngleXU=0 Radius=1
    g44: Circle CenterX=127.326 CenterY=56.7187 CenterZ=0 NormalX=0 NormalY=0 NormalZ=1 AngleXU=0 Radius=1
    g45: BSplineCurve PolesCount=3 KnotsCount=2 Degree=2 IsPeriodic=0
    g46: GeomPoint X=125.607 Y=54.1951 Z=0
    g47: GeomPoint X=127.326 Y=56.7187 Z=0
    g48: Circle CenterX=236.821 CenterY=56.7187 CenterZ=0 NormalX=0 NormalY=0 NormalZ=1 AngleXU=0 Radius=1
    g49: Circle CenterX=224.513 CenterY=46.4944 CenterZ=0 NormalX=0 NormalY=0 NormalZ=1 AngleXU=0 Radius=1
    g50: Circle CenterX=238.538 CenterY=54.1951 CenterZ=0 NormalX=0 NormalY=0 NormalZ=1 AngleXU=0 Radius=1
    g51: BSplineCurve PolesCount=3 KnotsCount=2 Degree=2 IsPeriodic=0
    g52: GeomPoint X=236.821 Y=56.7187 Z=0
    g53: GeomPoint X=238.538 Y=54.1951 Z=0
    g54: Circle CenterX=238.538 CenterY=-21.7539 CenterZ=0 NormalX=0 NormalY=0 NormalZ=1 AngleXU=0 Radius=1
    g55: Circle CenterX=224.513 CenterY=-14.0532 CenterZ=0 NormalX=0 NormalY=0 NormalZ=1 AngleXU=0 Radius=1
    g56: Circle CenterX=236.821 CenterY=-24.2775 CenterZ=0 NormalX=0 NormalY=0 NormalZ=1 AngleXU=0 Radius=1
    g57: BSplineCurve PolesCount=3 KnotsCount=2 Degree=2 IsPeriodic=0
    g58: GeomPoint X=238.538 Y=-21.7539 Z=0
    g59: GeomPoint X=236.821 Y=-24.2775 Z=0
    g60: Circle CenterX=125.607 CenterY=-21.7539 CenterZ=0 NormalX=0 NormalY=0 NormalZ=1 AngleXU=0 Radius=1
    g61: Circle CenterX=139.632 CenterY=-14.0532 CenterZ=0 NormalX=0 NormalY=0 NormalZ=1 AngleXU=0 Radius=1
    g62: Circle CenterX=127.325 CenterY=-24.2775 CenterZ=0 NormalX=0 NormalY=0 NormalZ=1 AngleXU=0 Radius=1
    g63: BSplineCurve PolesCount=3 KnotsCount=2 Degree=2 IsPeriodic=0
    g64: GeomPoint X=125.607 Y=-21.7539 Z=0
    g65: GeomPoint X=127.325 Y=-24.2775 Z=0
    g66: Circle CenterX=302.996 CenterY=111.695 CenterZ=0 NormalX=0 NormalY=0 NormalZ=1 AngleXU=0 Radius=1
    g67: Circle CenterX=306.073 CenterY=114.251 CenterZ=0 NormalX=0 NormalY=0 NormalZ=1 AngleXU=0 Radius=1
    g68: Circle CenterX=306.073 CenterY=110.251 CenterZ=0 NormalX=0 NormalY=0 NormalZ=1 AngleXU=0 Radius=1
    g69: BSplineCurve PolesCount=3 KnotsCount=2 Degree=2 IsPeriodic=0
    g70: GeomPoint X=302.996 Y=111.695 Z=0
    g71: GeomPoint X=306.073 Y=110.251 Z=0
    g72: Circle CenterX=306.073 CenterY=95.2763 CenterZ=0 NormalX=0 NormalY=0 NormalZ=1 AngleXU=0 Radius=1
    g73: Circle CenterX=306.073 CenterY=91.2763 CenterZ=0 NormalX=0 NormalY=0 NormalZ=1 AngleXU=0 Radius=1
    g74: Circle CenterX=302.567 CenterY=89.3511 CenterZ=0 NormalX=0 NormalY=0 NormalZ=1 AngleXU=0 Radius=1
    g75: BSplineCurve PolesCount=3 KnotsCount=2 Degree=2 IsPeriodic=0
    g76: GeomPoint X=306.073 Y=95.2763 Z=0
    g77: GeomPoint X=302.567 Y=89.3511 Z=0
    g78: LineSegment StartX=306.073 StartY=110.251 StartZ=0 EndX=306.073 EndY=95.2763 EndZ=0
    g79: LineSegment StartX=302.996 StartY=111.695 StartZ=0 EndX=236.821 EndY=56.7187 EndZ=0
    g80: LineSegment StartX=238.538 StartY=54.1951 StartZ=0 EndX=302.567 EndY=89.3511 EndZ=0
    g81: Circle CenterX=61.1496 CenterY=111.695 CenterZ=0 NormalX=0 NormalY=0 NormalZ=1 AngleXU=0 Radius=1
    g82: Circle CenterX=58.0728 CenterY=114.251 CenterZ=0 NormalX=0 NormalY=0 NormalZ=1 AngleXU=0 Radius=1
    g83: Circle CenterX=58.0728 CenterY=110.251 CenterZ=0 NormalX=0 NormalY=0 NormalZ=1 AngleXU=0 Radius=1
    g84: BSplineCurve PolesCount=3 KnotsCount=2 Degree=2 IsPeriodic=0
    g85: GeomPoint X=61.1496 Y=111.695 Z=0
    g86: GeomPoint X=58.0728 Y=110.251 Z=0
    g87: Circle CenterX=61.5791 CenterY=89.3511 CenterZ=0 NormalX=0 NormalY=0 NormalZ=1 AngleXU=0 Radius=1
    g88: Circle CenterX=58.0728 CenterY=91.2763 CenterZ=0 NormalX=0 NormalY=0 NormalZ=1 AngleXU=0 Radius=1
    g89: Circle CenterX=58.0728 CenterY=95.2763 CenterZ=0 NormalX=0 NormalY=0 NormalZ=1 AngleXU=0 Radius=1
    g90: BSplineCurve PolesCount=3 KnotsCount=2 Degree=2 IsPeriodic=0
    g91: GeomPoint X=61.5791 Y=89.3511 Z=0
    g92: GeomPoint X=58.0728 Y=95.2763 Z=0
    g93: LineSegment StartX=58.0728 StartY=110.251 StartZ=0 EndX=58.0728 EndY=95.2763 EndZ=0
    g94: LineSegment StartX=61.1496 StartY=111.695 StartZ=0 EndX=127.326 EndY=56.7187 EndZ=0
    g95: LineSegment StartX=125.607 StartY=54.1951 StartZ=0 EndX=61.5791 EndY=89.3511 EndZ=0
    g96: Circle CenterX=61.5791 CenterY=-56.9099 CenterZ=0 NormalX=0 NormalY=0 NormalZ=1 AngleXU=0 Radius=1
    g97: Circle CenterX=58.0728 CenterY=-58.8351 CenterZ=0 NormalX=0 NormalY=0 NormalZ=1 AngleXU=0 Radius=1
    g98: Circle CenterX=58.0728 CenterY=-62.8351 CenterZ=0 NormalX=0 NormalY=0 NormalZ=1 AngleXU=0 Radius=1
    g99: BSplineCurve PolesCount=3 KnotsCount=2 Degree=2 IsPeriodic=0
    g100: GeomPoint X=61.5791 Y=-56.9099 Z=0
    g101: GeomPoint X=58.0728 Y=-62.8351 Z=0
    g102: Circle CenterX=58.0728 CenterY=-77.8102 CenterZ=0 NormalX=0 NormalY=0 NormalZ=1 AngleXU=0 Radius=1
    g103: Circle CenterX=58.0728 CenterY=-81.8102 CenterZ=0 NormalX=0 NormalY=0 NormalZ=1 AngleXU=0 Radius=1
    g104: Circle CenterX=61.1496 CenterY=-79.2541 CenterZ=0 NormalX=0 NormalY=0 NormalZ=1 AngleXU=0 Radius=1
    g105: BSplineCurve PolesCount=3 KnotsCount=2 Degree=2 IsPeriodic=0
    g106: GeomPoint X=58.0728 Y=-77.8102 Z=0
    g107: GeomPoint X=61.1496 Y=-79.2541 Z=0
    g108: LineSegment StartX=58.0728 StartY=-62.8351 StartZ=0 EndX=58.0728 EndY=-77.8102 EndZ=0
    g109: LineSegment StartX=61.1496 StartY=-79.2541 StartZ=0 EndX=127.325 EndY=-24.2775 EndZ=0
    g110: LineSegment StartX=125.607 StartY=-21.7539 StartZ=0 EndX=61.5791 EndY=-56.9099 EndZ=0
    g111: Circle CenterX=302.567 CenterY=-56.9099 CenterZ=0 NormalX=0 NormalY=0 NormalZ=1 AngleXU=0 Radius=1
    g112: Circle CenterX=306.073 CenterY=-58.8351 CenterZ=0 NormalX=0 NormalY=0 NormalZ=1 AngleXU=0 Radius=1
    g113: Circle CenterX=306.073 CenterY=-62.8351 CenterZ=0 NormalX=0 NormalY=0 NormalZ=1 AngleXU=0 Radius=1
    g114: BSplineCurve PolesCount=3 KnotsCount=2 Degree=2 IsPeriodic=0
    g115: GeomPoint X=302.567 Y=-56.9099 Z=0
    g116: GeomPoint X=306.073 Y=-62.8351 Z=0
    g117: Circle CenterX=302.996 CenterY=-79.2541 CenterZ=0 NormalX=0 NormalY=0 NormalZ=1 AngleXU=0 Radius=1
    g118: Circle CenterX=306.073 CenterY=-81.8102 CenterZ=0 NormalX=0 NormalY=0 NormalZ=1 AngleXU=0 Radius=1
    g119: Circle CenterX=306.073 CenterY=-77.8102 CenterZ=0 NormalX=0 NormalY=0 NormalZ=1 AngleXU=0 Radius=1
    g120: BSplineCurve PolesCount=3 KnotsCount=2 Degree=2 IsPeriodic=0
    g121: GeomPoint X=302.996 Y=-79.2541 Z=0
    g122: GeomPoint X=306.073 Y=-77.8102 Z=0
    g123: LineSegment StartX=306.073 StartY=-62.8351 StartZ=0 EndX=306.073 EndY=-77.8102 EndZ=0
    g124: LineSegment StartX=302.996 StartY=-79.2541 StartZ=0 EndX=236.821 EndY=-24.2775 EndZ=0
    g125: LineSegment StartX=238.538 StartY=-21.7539 StartZ=0 EndX=302.567 EndY=-56.9099 EndZ=0
    g126: Circle CenterX=61.6457 CenterY=-88.8112 CenterZ=0 NormalX=0 NormalY=0 NormalZ=1 AngleXU=0 Radius=1
    g127: Circle CenterX=58.0728 CenterY=-91.7794 CenterZ=0 NormalX=0 NormalY=0 NormalZ=1 AngleXU=0 Radius=1
    g128: Circle CenterX=63.9135 CenterY=-91.7794 CenterZ=0 NormalX=0 NormalY=0 NormalZ=1 AngleXU=0 Radius=1
    g129: BSplineCurve PolesCount=3 KnotsCount=2 Degree=2 IsPeriodic=0
    g130: GeomPoint X=61.6457 Y=-88.8112 Z=0
    g131: GeomPoint X=63.9135 Y=-91.7794 Z=0
    g132: Circle CenterX=179.022 CenterY=-85.8163 CenterZ=0 NormalX=0 NormalY=0 NormalZ=1 AngleXU=0 Radius=1
    g133: Circle CenterX=179.022 CenterY=-91.7794 CenterZ=0 NormalX=0 NormalY=0 NormalZ=1 AngleXU=0 Radius=1
    g134: Circle CenterX=171.895 CenterY=-91.7794 CenterZ=0 NormalX=0 NormalY=0 NormalZ=1 AngleXU=0 Radius=1
    g135: BSplineCurve PolesCount=3 KnotsCount=2 Degree=2 IsPeriodic=0
    g136: GeomPoint X=179.022 Y=-85.8163 Z=0
    g137: GeomPoint X=171.895 Y=-91.7794 Z=0
    g138: Circle CenterX=185.124 CenterY=-86.2028 CenterZ=0 NormalX=0 NormalY=0 NormalZ=1 AngleXU=0 Radius=1
    g139: Circle CenterX=185.124 CenterY=-91.7794 CenterZ=0 NormalX=0 NormalY=0 NormalZ=1 AngleXU=0 Radius=1
    g140: Circle CenterX=191.747 CenterY=-91.7794 CenterZ=0 NormalX=0 NormalY=0 NormalZ=1 AngleXU=0 Radius=1
    g141: BSplineCurve PolesCount=3 KnotsCount=2 Degree=2 IsPeriodic=0
    g142: GeomPoint X=185.124 Y=-86.2028 Z=0
    g143: GeomPoint X=191.747 Y=-91.7794 Z=0
    g144: Circle CenterX=299.888 CenterY=-86.6413 CenterZ=0 NormalX=0 NormalY=0 NormalZ=1 AngleXU=0 Radius=1
    g145: Circle CenterX=306.073 CenterY=-91.7794 CenterZ=0 NormalX=0 NormalY=0 NormalZ=1 AngleXU=0 Radius=1
    g146: Circle CenterX=298.776 CenterY=-91.7794 CenterZ=0 NormalX=0 NormalY=0 NormalZ=1 AngleXU=0 Radius=1
    g147: BSplineCurve PolesCount=3 KnotsCount=2 Degree=2 IsPeriodic=0
    g148: GeomPoint X=299.888 Y=-86.6413 Z=0
    g149: GeomPoint X=298.776 Y=-91.7794 Z=0
    g150: LineSegment StartX=189.124 StartY=5.37834 StartZ=0 EndX=299.888 EndY=-86.6413 EndZ=0
    g151: LineSegment StartX=298.776 StartY=-91.7794 StartZ=0 EndX=191.747 EndY=-91.7794 EndZ=0
    g152: LineSegment StartX=185.124 StartY=-86.2028 StartZ=0 EndX=185.124 EndY=5.34704 EndZ=0
    g153: LineSegment StartX=179.022 StartY=5.34704 StartZ=0 EndX=179.022 EndY=-85.8163 EndZ=0
    g154: LineSegment StartX=171.895 StartY=-91.7794 StartZ=0 EndX=63.9135 EndY=-91.7794 EndZ=0
    g155: LineSegment StartX=61.6457 StartY=-88.8112 StartZ=0 EndX=175.022 EndY=5.37834 EndZ=0
    g156: Circle CenterX=302.073 CenterY=124.221 CenterZ=0 NormalX=0 NormalY=0 NormalZ=1 AngleXU=0 Radius=1
    g157: Circle CenterX=306.073 CenterY=124.221 CenterZ=0 NormalX=0 NormalY=0 NormalZ=1 AngleXU=0 Radius=1
    g158: Circle CenterX=302.996 CenterY=121.665 CenterZ=0 NormalX=0 NormalY=0 NormalZ=1 AngleXU=0 Radius=1
    g159: BSplineCurve PolesCount=3 KnotsCount=2 Degree=2 IsPeriodic=0
    g160: GeomPoint X=302.073 Y=124.221 Z=0
    g161: GeomPoint X=302.996 Y=121.665 Z=0
    g162: Circle CenterX=189.124 CenterY=124.221 CenterZ=0 NormalX=0 NormalY=0 NormalZ=1 AngleXU=0 Radius=1
    g163: Circle CenterX=185.124 CenterY=124.221 CenterZ=0 NormalX=0 NormalY=0 NormalZ=1 AngleXU=0 Radius=1
    g164: Circle CenterX=185.124 CenterY=120.221 CenterZ=0 NormalX=0 NormalY=0 NormalZ=1 AngleXU=0 Radius=1
    g165: BSplineCurve PolesCount=3 KnotsCount=2 Degree=2 IsPeriodic=0
    g166: GeomPoint X=189.124 Y=124.221 Z=0
    g167: GeomPoint X=185.124 Y=120.221 Z=0
    g168: Circle CenterX=175.022 CenterY=124.221 CenterZ=0 NormalX=0 NormalY=0 NormalZ=1 AngleXU=0 Radius=1
    g169: Circle CenterX=179.022 CenterY=124.221 CenterZ=0 NormalX=0 NormalY=0 NormalZ=1 AngleXU=0 Radius=1
    g170: Circle CenterX=179.022 CenterY=120.221 CenterZ=0 NormalX=0 NormalY=0 NormalZ=1 AngleXU=0 Radius=1
    g171: BSplineCurve PolesCount=3 KnotsCount=2 Degree=2 IsPeriodic=0
    g172: GeomPoint X=175.022 Y=124.221 Z=0
    g173: GeomPoint X=179.022 Y=120.221 Z=0
    g174: Circle CenterX=62.0728 CenterY=124.221 CenterZ=0 NormalX=0 NormalY=0 NormalZ=1 AngleXU=0 Radius=1
    g175: Circle CenterX=58.0728 CenterY=124.221 CenterZ=0 NormalX=0 NormalY=0 NormalZ=1 AngleXU=0 Radius=1
    g176: Circle CenterX=61.1496 CenterY=121.665 CenterZ=0 NormalX=0 NormalY=0 NormalZ=1 AngleXU=0 Radius=1
    g177: BSplineCurve PolesCount=3 KnotsCount=2 Degree=2 IsPeriodic=0
    g178: GeomPoint X=62.0728 Y=124.221 Z=0
    g179: GeomPoint X=61.1496 Y=121.665 Z=0
    g180: LineSegment StartX=62.0728 StartY=124.221 StartZ=0 EndX=175.022 EndY=124.221 EndZ=0
    g181: LineSegment StartX=179.022 StartY=120.221 StartZ=0 EndX=179.022 EndY=27.0628 EndZ=0
    g182: LineSegment StartX=185.124 StartY=27.0628 StartZ=0 EndX=185.124 EndY=120.221 EndZ=0
    g183: LineSegment StartX=189.124 StartY=124.221 StartZ=0 EndX=302.073 EndY=124.221 EndZ=0
    g184: LineSegment StartX=302.996 StartY=121.665 StartZ=0 EndX=189.124 EndY=27.0628 EndZ=0
    g185: LineSegment StartX=175.022 StartY=27.0628 StartZ=0 EndX=61.1496 EndY=121.665 EndZ=0
    g186: Circle CenterX=61.5791 CenterY=75.4095 CenterZ=0 NormalX=0 NormalY=0 NormalZ=1 AngleXU=0 Radius=1
    g187: Circle CenterX=58.0728 CenterY=77.3346 CenterZ=0 NormalX=0 NormalY=0 NormalZ=1 AngleXU=0 Radius=1
    g188: Circle CenterX=58.0728 CenterY=73.3346 CenterZ=0 NormalX=0 NormalY=0 NormalZ=1 AngleXU=0 Radius=1
    g189: BSplineCurve PolesCount=3 KnotsCount=2 Degree=2 IsPeriodic=0
    g190: GeomPoint X=61.5791 Y=75.4095 Z=0
    g191: GeomPoint X=58.0728 Y=73.3346 Z=0
    g192: Circle CenterX=58.0728 CenterY=-40.8935 CenterZ=0 NormalX=0 NormalY=0 NormalZ=1 AngleXU=0 Radius=1
    g193: Circle CenterX=58.0728 CenterY=-44.8935 CenterZ=0 NormalX=0 NormalY=0 NormalZ=1 AngleXU=0 Radius=1
    g194: Circle CenterX=61.5791 CenterY=-42.9683 CenterZ=0 NormalX=0 NormalY=0 NormalZ=1 AngleXU=0 Radius=1
    g195: BSplineCurve PolesCount=3 KnotsCount=2 Degree=2 IsPeriodic=0
    g196: GeomPoint X=58.0728 Y=-40.8935 Z=0
    g197: GeomPoint X=61.5791 Y=-42.9683 Z=0
    g198: LineSegment StartX=61.5791 StartY=-42.9683 StartZ=0 EndX=165.871 EndY=14.2954 EndZ=0
    g199: LineSegment StartX=165.871 StartY=18.1458 StartZ=0 EndX=61.5791 EndY=75.4095 EndZ=0
    g200: LineSegment StartX=58.0728 StartY=73.3346 StartZ=0 EndX=58.0728 EndY=-40.8935 EndZ=0
    g201: Circle CenterX=302.567 CenterY=-42.9683 CenterZ=0 NormalX=0 NormalY=0 NormalZ=1 AngleXU=0 Radius=1
    g202: Circle CenterX=306.073 CenterY=-44.8935 CenterZ=0 NormalX=0 NormalY=0 NormalZ=1 AngleXU=0 Radius=1
    g203: Circle CenterX=306.073 CenterY=-40.8935 CenterZ=0 NormalX=0 NormalY=0 NormalZ=1 AngleXU=0 Radius=1
    g204: BSplineCurve PolesCount=3 KnotsCount=2 Degree=2 IsPeriodic=0
    g205: GeomPoint X=302.567 Y=-42.9683 Z=0
    g206: GeomPoint X=306.073 Y=-40.8935 Z=0
    g207: Circle CenterX=306.073 CenterY=73.3346 CenterZ=0 NormalX=0 NormalY=0 NormalZ=1 AngleXU=0 Radius=1
    g208: Circle CenterX=306.073 CenterY=77.3346 CenterZ=0 NormalX=0 NormalY=0 NormalZ=1 AngleXU=0 Radius=1
    g209: Circle CenterX=302.567 CenterY=75.4095 CenterZ=0 NormalX=0 NormalY=0 NormalZ=1 AngleXU=0 Radius=1
    g210: BSplineCurve PolesCount=3 KnotsCount=2 Degree=2 IsPeriodic=0
    g211: GeomPoint X=306.073 Y=73.3346 Z=0
    g212: GeomPoint X=302.567 Y=75.4095 Z=0
    g213: LineSegment StartX=302.567 StartY=-42.9683 StartZ=0 EndX=198.275 EndY=14.2954 EndZ=0
    g214: LineSegment StartX=198.275 StartY=18.1458 StartZ=0 EndX=302.567 EndY=75.4095 EndZ=0
    g215: LineSegment StartX=306.073 StartY=73.3346 StartZ=0 EndX=306.073 EndY=-40.8935 EndZ=0
    g216: LineSegment StartX=322.073 StartY=105.865 StartZ=0 EndX=328.643 EndY=105.865 EndZ=0
    g217: LineSegment StartX=318.073 StartY=120.221 StartZ=0 EndX=318.073 EndY=109.865 EndZ=0
    g218: LineSegment StartX=336.157 StartY=107.779 StartZ=0 EndX=362.567 EndY=122.294 EndZ=0
    g219: Circle CenterX=362.073 CenterY=124.221 CenterZ=0 NormalX=0 NormalY=0 NormalZ=1 AngleXU=0 Radius=1
    g220: Circle CenterX=366.073 CenterY=124.221 CenterZ=0 NormalX=0 NormalY=0 NormalZ=1 AngleXU=0 Radius=1
    g221: Circle CenterX=362.567 CenterY=122.294 CenterZ=0 NormalX=0 NormalY=0 NormalZ=1 AngleXU=0 Radius=1
    g222: BSplineCurve PolesCount=3 KnotsCount=2 Degree=2 IsPeriodic=0
    g223: GeomPoint X=362.073 Y=124.221 Z=0
    g224: GeomPoint X=362.567 Y=122.294 Z=0
    g225: Circle CenterX=322.073 CenterY=124.221 CenterZ=0 NormalX=0 NormalY=0 NormalZ=1 AngleXU=0 Radius=1
    g226: Circle CenterX=318.073 CenterY=124.221 CenterZ=0 NormalX=0 NormalY=0 NormalZ=1 AngleXU=0 Radius=1
    g227: Circle CenterX=318.073 CenterY=120.221 CenterZ=0 NormalX=0 NormalY=0 NormalZ=1 AngleXU=0 Radius=1
    g228: BSplineCurve PolesCount=3 KnotsCount=2 Degree=2 IsPeriodic=0
    g229: GeomPoint X=322.073 Y=124.221 Z=0
    g230: GeomPoint X=318.073 Y=120.221 Z=0
    g231: Circle CenterX=322.073 CenterY=105.865 CenterZ=0 NormalX=0 NormalY=0 NormalZ=1 AngleXU=0 Radius=1
    g232: Circle CenterX=318.073 CenterY=105.865 CenterZ=0 NormalX=0 NormalY=0 NormalZ=1 AngleXU=0 Radius=1
    g233: Circle CenterX=318.073 CenterY=109.865 CenterZ=0 NormalX=0 NormalY=0 NormalZ=1 AngleXU=0 Radius=1
    g234: BSplineCurve PolesCount=3 KnotsCount=2 Degree=2 IsPeriodic=0
    g235: GeomPoint X=322.073 Y=105.865 Z=0
    g236: GeomPoint X=318.073 Y=109.865 Z=0
    g237: Circle CenterX=336.157 CenterY=107.779 CenterZ=0 NormalX=0 NormalY=0 NormalZ=1 AngleXU=0 Radius=1
    g238: Circle CenterX=332.651 CenterY=105.853 CenterZ=0 NormalX=0 NormalY=0 NormalZ=1 AngleXU=0 Radius=1
    g239: Circle CenterX=328.643 CenterY=105.865 CenterZ=0 NormalX=0 NormalY=0 NormalZ=1 AngleXU=0 Radius=1
    g240: BSplineCurve PolesCount=3 KnotsCount=2 Degree=2 IsPeriodic=0
    g241: GeomPoint X=336.157 Y=107.779 Z=0
    g242: GeomPoint X=328.643 Y=105.865 Z=0
    g243: LineSegment StartX=322.073 StartY=124.221 StartZ=0 EndX=362.073 EndY=124.221 EndZ=0
    g244: Circle CenterX=371.567 CenterY=-80.8644 CenterZ=0 NormalX=0 NormalY=0 NormalZ=1 AngleXU=0 Radius=1
    g245: Circle CenterX=375.073 CenterY=-82.7896 CenterZ=0 NormalX=0 NormalY=0 NormalZ=1 AngleXU=0 Radius=1
    g246: Circle CenterX=375.073 CenterY=-78.7896 CenterZ=0 NormalX=0 NormalY=0 NormalZ=1 AngleXU=0 Radius=1
    g247: BSplineCurve PolesCount=3 KnotsCount=2 Degree=2 IsPeriodic=0
    g248: GeomPoint X=371.567 Y=-80.8644 Z=0
    g249: GeomPoint X=375.073 Y=-78.7896 Z=0
    g250: Circle CenterX=321.579 CenterY=-53.4075 CenterZ=0 NormalX=0 NormalY=0 NormalZ=1 AngleXU=0 Radius=1
    g251: Circle CenterX=318.073 CenterY=-51.4823 CenterZ=0 NormalX=0 NormalY=0 NormalZ=1 AngleXU=0 Radius=1
    g252: Circle CenterX=318.073 CenterY=-47.4805 CenterZ=0 NormalX=0 NormalY=0 NormalZ=1 AngleXU=0 Radius=1
    g253: BSplineCurve PolesCount=3 KnotsCount=2 Degree=2 IsPeriodic=0
    g254: GeomPoint X=321.579 Y=-53.4075 Z=0
    g255: GeomPoint X=318.073 Y=-47.4805 Z=0
    g256: LineSegment StartX=371.567 StartY=-80.8644 StartZ=0 EndX=321.579 EndY=-53.4075 EndZ=0
    g257: Circle CenterX=321.579 CenterY=-67.3492 CenterZ=0 NormalX=0 NormalY=0 NormalZ=1 AngleXU=0 Radius=1
    g258: Circle CenterX=318.073 CenterY=-65.424 CenterZ=0 NormalX=0 NormalY=0 NormalZ=1 AngleXU=0 Radius=1
    g259: Circle CenterX=318.073 CenterY=-69.424 CenterZ=0 NormalX=0 NormalY=0 NormalZ=1 AngleXU=0 Radius=1
    g260: BSplineCurve PolesCount=3 KnotsCount=2 Degree=2 IsPeriodic=0
    g261: GeomPoint X=321.579 Y=-67.3492 Z=0
    g262: GeomPoint X=318.073 Y=-69.424 Z=0
    g263: Circle CenterX=362.567 CenterY=-89.8542 CenterZ=0 NormalX=0 NormalY=0 NormalZ=1 AngleXU=0 Radius=1
    g264: Circle CenterX=366.073 CenterY=-91.7794 CenterZ=0 NormalX=0 NormalY=0 NormalZ=1 AngleXU=0 Radius=1
    g265: Circle CenterX=362.073 CenterY=-91.7794 CenterZ=0 NormalX=0 NormalY=0 NormalZ=1 AngleXU=0 Radius=1
    g266: BSplineCurve PolesCount=3 KnotsCount=2 Degree=2 IsPeriodic=0
    g267: GeomPoint X=362.567 Y=-89.8542 Z=0
    g268: GeomPoint X=362.073 Y=-91.7794 Z=0
    g269: Circle CenterX=322.073 CenterY=-91.7794 CenterZ=0 NormalX=0 NormalY=0 NormalZ=1 AngleXU=0 Radius=1
    g270: Circle CenterX=318.073 CenterY=-91.7794 CenterZ=0 NormalX=0 NormalY=0 NormalZ=1 AngleXU=0 Radius=1
    g271: Circle CenterX=318.073 CenterY=-87.7794 CenterZ=0 NormalX=0 NormalY=0 NormalZ=1 AngleXU=0 Radius=1
    g272: BSplineCurve PolesCount=3 KnotsCount=2 Degree=2 IsPeriodic=0
    g273: GeomPoint X=322.073 Y=-91.7794 Z=0
    g274: GeomPoint X=318.073 Y=-87.7794 Z=0
    g275: LineSegment StartX=362.567 StartY=-89.8542 StartZ=0 EndX=321.579 EndY=-67.3492 EndZ=0
    g276: LineSegment StartX=318.073 StartY=-69.424 StartZ=0 EndX=318.073 EndY=-87.7794 EndZ=0
    g277: LineSegment StartX=322.073 StartY=-91.7794 StartZ=0 EndX=362.073 EndY=-91.7794 EndZ=0
    g278: Circle CenterX=2.07281 CenterY=124.221 CenterZ=0 NormalX=0 NormalY=0 NormalZ=1 AngleXU=0 Radius=1
    g279: Circle CenterX=1.57905 CenterY=122.295 CenterZ=0 NormalX=0 NormalY=0 NormalZ=1 AngleXU=0 Radius=1
    g280: BSplineCurve PolesCount=3 KnotsCount=2 Degree=2 IsPeriodic=0
    g281: GeomPoint X=2.07281 Y=124.221 Z=0
    g282: GeomPoint X=1.57905 Y=122.295 Z=0
    g283: Circle CenterX=42.0728 CenterY=124.221 CenterZ=0 NormalX=0 NormalY=0 NormalZ=1 AngleXU=0 Radius=1
    g284: Circle CenterX=46.0728 CenterY=124.221 CenterZ=0 NormalX=0 NormalY=0 NormalZ=1 AngleXU=0 Radius=1
    g285: Circle CenterX=46.0728 CenterY=120.221 CenterZ=0 NormalX=0 NormalY=0 NormalZ=1 AngleXU=0 Radius=1
    g286: BSplineCurve PolesCount=3 KnotsCount=2 Degree=2 IsPeriodic=0
    g287: GeomPoint X=42.0728 Y=124.221 Z=0
    g288: GeomPoint X=46.0728 Y=120.221 Z=0
    g289: Circle CenterX=46.0728 CenterY=109.865 CenterZ=0 NormalX=0 NormalY=0 NormalZ=1 AngleXU=0 Radius=1
    g290: Circle CenterX=46.0728 CenterY=105.865 CenterZ=0 NormalX=0 NormalY=0 NormalZ=1 AngleXU=0 Radius=1
    g291: Circle CenterX=42.0728 CenterY=105.865 CenterZ=0 NormalX=0 NormalY=0 NormalZ=1 AngleXU=0 Radius=1
    g292: BSplineCurve PolesCount=3 KnotsCount=2 Degree=2 IsPeriodic=0
    g293: GeomPoint X=46.0728 Y=109.865 Z=0
    g294: GeomPoint X=42.0728 Y=105.865 Z=0
    g295: Circle CenterX=35.5028 CenterY=105.865 CenterZ=0 NormalX=0 NormalY=0 NormalZ=1 AngleXU=0 Radius=1
    g296: Circle CenterX=31.5028 CenterY=105.865 CenterZ=0 NormalX=0 NormalY=0 NormalZ=1 AngleXU=0 Radius=1
    g297: Circle CenterX=27.9965 CenterY=107.79 CenterZ=0 NormalX=0 NormalY=0 NormalZ=1 AngleXU=0 Radius=1
    g298: BSplineCurve PolesCount=3 KnotsCount=2 Degree=2 IsPeriodic=0
    g299: GeomPoint X=35.5028 Y=105.865 Z=0
    g300: GeomPoint X=27.9965 Y=107.79 Z=0
    g301: LineSegment StartX=2.07281 StartY=124.221 StartZ=0 EndX=42.0728 EndY=124.221 EndZ=0
    g302: LineSegment StartX=46.0728 StartY=120.221 StartZ=0 EndX=46.0728 EndY=109.865 EndZ=0
    g303: LineSegment StartX=42.0728 StartY=105.865 StartZ=0 EndX=35.5028 EndY=105.865 EndZ=0
    g304: LineSegment StartX=27.9965 StartY=107.79 StartZ=0 EndX=1.57905 EndY=122.295 EndZ=0
    g305: Circle CenterX=42.5666 CenterY=-67.3492 CenterZ=0 NormalX=0 NormalY=0 NormalZ=1 AngleXU=0 Radius=1
    g306: Circle CenterX=46.0728 CenterY=-65.424 CenterZ=0 NormalX=0 NormalY=0 NormalZ=1 AngleXU=0 Radius=1
    g307: Circle CenterX=46.0728 CenterY=-69.424 CenterZ=0 NormalX=0 NormalY=0 NormalZ=1 AngleXU=0 Radius=1
    g308: BSplineCurve PolesCount=3 KnotsCount=2 Degree=2 IsPeriodic=0
    g309: GeomPoint X=42.5666 Y=-67.3492 Z=0
    g310: GeomPoint X=46.0728 Y=-69.424 Z=0
    g311: Circle CenterX=46.0728 CenterY=-87.7794 CenterZ=0 NormalX=0 NormalY=0 NormalZ=1 AngleXU=0 Radius=1
    g312: Circle CenterX=46.0728 CenterY=-91.7794 CenterZ=0 NormalX=0 NormalY=0 NormalZ=1 AngleXU=0 Radius=1
    g313: Circle CenterX=42.0728 CenterY=-91.7794 CenterZ=0 NormalX=0 NormalY=0 NormalZ=1 AngleXU=0 Radius=1
    g314: BSplineCurve PolesCount=3 KnotsCount=2 Degree=2 IsPeriodic=0
    g315: GeomPoint X=46.0728 Y=-87.7794 Z=0
    g316: GeomPoint X=42.0728 Y=-91.7794 Z=0
    g317: Circle CenterX=2.07281 CenterY=-91.7794 CenterZ=0 NormalX=0 NormalY=0 NormalZ=1 AngleXU=0 Radius=1
    g318: Circle CenterX=-1.92719 CenterY=-91.7794 CenterZ=0 NormalX=0 NormalY=0 NormalZ=1 AngleXU=0 Radius=1
    g319: Circle CenterX=1.57905 CenterY=-89.8542 CenterZ=0 NormalX=0 NormalY=0 NormalZ=1 AngleXU=0 Radius=1
    g320: BSplineCurve PolesCount=3 KnotsCount=2 Degree=2 IsPeriodic=0
    g321: GeomPoint X=2.07281 Y=-91.7794 Z=0
    g322: GeomPoint X=1.57905 Y=-89.8542 Z=0
    g323: LineSegment StartX=2.07281 StartY=-91.7794 StartZ=0 EndX=42.0728 EndY=-91.7794 EndZ=0
    g324: LineSegment StartX=46.0728 StartY=-87.7794 StartZ=0 EndX=46.0728 EndY=-69.424 EndZ=0
    g325: LineSegment StartX=42.5666 StartY=-67.3492 StartZ=0 EndX=1.57905 EndY=-89.8542 EndZ=0
    g326: Circle CenterX=322.073 CenterY=76.4095 CenterZ=0 NormalX=0 NormalY=0 NormalZ=1 AngleXU=0 Radius=4
    g327: BSplineCurve PolesCount=3 KnotsCount=2 Degree=2 IsPeriodic=0
    g328: GeomPoint X=318.073 Y=72.4095 Z=0
    g329: GeomPoint X=322.073 Y=76.4095 Z=0
    g330: Circle CenterX=375.073 CenterY=72.4095 CenterZ=0 NormalX=0 NormalY=0 NormalZ=1 AngleXU=0 Radius=1
    g331: Circle CenterX=375.073 CenterY=76.4095 CenterZ=0 NormalX=0 NormalY=0 NormalZ=1 AngleXU=0 Radius=1
    g332: Circle CenterX=371.073 CenterY=76.4095 CenterZ=0 NormalX=0 NormalY=0 NormalZ=1 AngleXU=0 Radius=1
    g333: BSplineCurve PolesCount=3 KnotsCount=2 Degree=2 IsPeriodic=0
    g334: GeomPoint X=375.073 Y=72.4095 Z=0
    g335: GeomPoint X=371.073 Y=76.4095 Z=0
    g336: LineSegment StartX=322.073 StartY=76.4095 StartZ=0 EndX=371.073 EndY=76.4095 EndZ=0
    g337: LineSegment StartX=318.073 StartY=72.4095 StartZ=0 EndX=318.073 EndY=-47.4805 EndZ=0
    g338: LineSegment StartX=375.073 StartY=72.4095 StartZ=0 EndX=375.073 EndY=-78.7896 EndZ=0
    g339: ArcOfCircle CenterX=-26.9272 CenterY=22.1087 CenterZ=0 NormalX=0 NormalY=0 NormalZ=1 AngleXU=0 Radius=4 StartAngle=5e-16 EndAngle=3.14159
    g340: LineSegment StartX=-22.9272 StartY=22.1087 StartZ=0 EndX=-18.9272 EndY=-83.7794 EndZ=0
    g341: LineSegment StartX=-34.9272 StartY=-83.7794 StartZ=0 EndX=-30.9272 EndY=22.1087 EndZ=0
    g342: ArcOfCircle CenterX=391.073 CenterY=22.1087 CenterZ=0 NormalX=0 NormalY=0 NormalZ=1 AngleXU=0 Radius=4 StartAngle=0 EndAngle=3.14159
    g343: LineSegment StartX=387.073 StartY=22.1087 StartZ=0 EndX=383.073 EndY=-83.7794 EndZ=0
    g344: LineSegment StartX=395.073 StartY=22.1087 StartZ=0 EndX=399.073 EndY=-83.7794 EndZ=0
    g345: Circle CenterX=-10.9272 CenterY=-78.7794 CenterZ=0 NormalX=0 NormalY=0 NormalZ=1 AngleXU=0 Radius=1
    g346: Circle CenterX=-10.9272 CenterY=-82.7794 CenterZ=0 NormalX=0 NormalY=0 NormalZ=1 AngleXU=0 Radius=1
    g347: Circle CenterX=-7.42095 CenterY=-80.8542 CenterZ=0 NormalX=0 NormalY=0 NormalZ=1 AngleXU=0 Radius=1
    g348: BSplineCurve PolesCount=3 KnotsCount=2 Degree=2 IsPeriodic=0
    g349: GeomPoint X=-10.9272 Y=-78.7794 Z=0
    g350: GeomPoint X=-7.42095 Y=-80.8542 Z=0
    g351: Circle CenterX=42.5666 CenterY=-53.4075 CenterZ=0 NormalX=0 NormalY=0 NormalZ=1 AngleXU=0 Radius=1
    g352: Circle CenterX=46.0728 CenterY=-51.4823 CenterZ=0 NormalX=0 NormalY=0 NormalZ=1 AngleXU=0 Radius=1
    g353: Circle CenterX=46.0728 CenterY=-47.4823 CenterZ=0 NormalX=0 NormalY=0 NormalZ=1 AngleXU=0 Radius=1
    g354: BSplineCurve PolesCount=3 KnotsCount=2 Degree=2 IsPeriodic=0
    g355: GeomPoint X=42.5666 Y=-53.4075 Z=0
    g356: GeomPoint X=46.0728 Y=-47.4823 Z=0
    g357: Circle CenterX=46.0728 CenterY=72.4095 CenterZ=0 NormalX=0 NormalY=0 NormalZ=1 AngleXU=0 Radius=1
    g358: Circle CenterX=46.0728 CenterY=76.4095 CenterZ=0 NormalX=0 NormalY=0 NormalZ=1 AngleXU=0 Radius=1
    g359: Circle CenterX=42.0728 CenterY=76.4095 CenterZ=0 NormalX=0 NormalY=0 NormalZ=1 AngleXU=0 Radius=1
    g360: BSplineCurve PolesCount=3 KnotsCount=2 Degree=2 IsPeriodic=0
    g361: GeomPoint X=46.0728 Y=72.4095 Z=0
    g362: GeomPoint X=42.0728 Y=76.4095 Z=0
    g363: Circle CenterX=-6.92718 CenterY=76.4095 CenterZ=0 NormalX=0 NormalY=0 NormalZ=1 AngleXU=0 Radius=1
    g364: Circle CenterX=-10.9272 CenterY=76.4095 CenterZ=0 NormalX=0 NormalY=0 NormalZ=1 AngleXU=0 Radius=1
    g365: Circle CenterX=-10.9272 CenterY=72.4095 CenterZ=0 NormalX=0 NormalY=0 NormalZ=1 AngleXU=0 Radius=1
    g366: BSplineCurve PolesCount=3 KnotsCount=2 Degree=2 IsPeriodic=0
    g367: GeomPoint X=-6.92718 Y=76.4095 Z=0
    g368: GeomPoint X=-10.9272 Y=72.4095 Z=0
    g369: LineSegment StartX=-10.9272 StartY=72.4095 StartZ=0 EndX=-10.9272 EndY=-78.7794 EndZ=0
    g370: LineSegment StartX=-7.42095 StartY=-80.8542 StartZ=0 EndX=42.5666 EndY=-53.4075 EndZ=0
    g371: LineSegment StartX=46.0728 StartY=-47.4823 StartZ=0 EndX=46.0728 EndY=72.4095 EndZ=0
    g372: LineSegment StartX=42.0728 StartY=76.4095 StartZ=0 EndX=-6.92719 EndY=76.4095 EndZ=0
  constraints (613):
    c: Vertical(g0)
    c: Vertical(g1)
    c: Block(g1)
    c: Block(g0)
    c: Weight(g4) = 1
    c: Equal(g4,g5)
    c: Equal(g4,g6)
    c: InternalAlignment(g4,g7)
    c: InternalAlignment(g5,g7)
    c: InternalAlignment(g6,g7)
    c: InternalAlignment(g8,g7)
    c: InternalAlignment(g9,g7)
    c: Weight(g10) = 1
    c: Equal(g10,g11)
    c: Equal(g10,g12)
    c: InternalAlignment(g10,g13)
    c: InternalAlignment(g11,g13)
    c: InternalAlignment(g12,g13)
    c: InternalAlignment(g14,g13)
    c: InternalAlignment(g15,g13)
    c: Block(g13)
    c: Block(g7)
    c: Weight(g16) = 1
    c: Equal(g16,g17)
    c: Equal(g16,g18)
    c: InternalAlignment(g16,g19)
    c: InternalAlignment(g17,g19)
    c: InternalAlignment(g18,g19)
    c: InternalAlignment(g20,g19)
    c: InternalAlignment(g21,g19)
    c: Weight(g22) = 1
    c: Equal(g22,g23)
    c: Equal(g22,g24)
    c: InternalAlignment(g22,g25)
    c: InternalAlignment(g23,g25)
    c: InternalAlignment(g24,g25)
    c: InternalAlignment(g26,g25)
    c: InternalAlignment(g27,g25)
    c: Block(g25)
    c: Block(g19)
    c: Weight(g28) = 1
    c: Equal(g28,g29)
    c: Equal(g28,g30)
    c: InternalAlignment(g28,g31)
    c: InternalAlignment(g29,g31)
    c: InternalAlignment(g30,g31)
    c: InternalAlignment(g32,g31)
    c: InternalAlignment(g33,g31)
    c: Weight(g34) = 1
    c: Equal(g34,g35)
    c: Equal(g34,g36)
    c: InternalAlignment(g34,g37)
    c: InternalAlignment(g35,g37)
    c: InternalAlignment(g36,g37)
    c: InternalAlignment(g38,g37)
    c: InternalAlignment(g39,g37)
    c: Block(g31)
    c: Block(g37)
    c: Coincident(g40,g1)
    c: Coincident(g40,g0)
    c: Horizontal(g40)
    c: Distance(g40) = 450
    c: Coincident(g41,g1)
    c: Coincident(g41,g0)
    c: Horizontal(g41)
    c: Weight(g42) = 1
    c: Equal(g42,g43)
    c: Equal(g42,g44)
    c: InternalAlignment(g42,g45)
    c: InternalAlignment(g43,g45)
    c: InternalAlignment(g44,g45)
    c: InternalAlignment(g46,g45)
    c: InternalAlignment(g47,g45)
    c: Block(g45)
    c: Weight(g48) = 1
    c: Equal(g48,g49)
    c: Equal(g48,g50)
    c: InternalAlignment(g48,g51)
    c: InternalAlignment(g49,g51)
    c: InternalAlignment(g50,g51)
    c: InternalAlignment(g52,g51)
    c: InternalAlignment(g53,g51)
    c: Block(g51)
    c: Weight(g54) = 1
    c: Equal(g54,g55)
    c: Equal(g54,g56)
    c: InternalAlignment(g54,g57)
    c: InternalAlignment(g55,g57)
    c: InternalAlignment(g56,g57)
    c: InternalAlignment(g58,g57)
    c: InternalAlignment(g59,g57)
    c: Block(g57)
    c: Weight(g60) = 1
    c: Equal(g60,g61)
    c: Equal(g60,g62)
    c: InternalAlignment(g60,g63)
    c: InternalAlignment(g61,g63)
    c: InternalAlignment(g62,g63)
    c: InternalAlignment(g64,g63)
    c: InternalAlignment(g65,g63)
    c: Block(g63)
    c: Weight(g66) = 1
    c: Equal(g66,g67)
    c: Equal(g66,g68)
    c: InternalAlignment(g66,g69)
    c: InternalAlignment(g67,g69)
    c: InternalAlignment(g68,g69)
    c: InternalAlignment(g70,g69)
    c: InternalAlignment(g71,g69)
    c: Weight(g72) = 1
    c: Equal(g72,g73)
    c: Equal(g72,g74)
    c: InternalAlignment(g72,g75)
    c: InternalAlignment(g73,g75)
    c: InternalAlignment(g74,g75)
    c: InternalAlignment(g76,g75)
    c: InternalAlignment(g77,g75)
    c: Block(g69)
    c: Block(g75)
    c: Coincident(g78,g69)
    c: Coincident(g78,g75)
    c: Vertical(g78)
    c: Coincident(g79,g69)
    c: Coincident(g79,g51)
    c: Coincident(g80,g51)
    c: Coincident(g80,g75)
    c: Weight(g81) = 1
    c: Equal(g81,g82)
    c: Equal(g81,g83)
    c: InternalAlignment(g81,g84)
    c: InternalAlignment(g82,g84)
    c: InternalAlignment(g83,g84)
    c: InternalAlignment(g85,g84)
    c: InternalAlignment(g86,g84)
    c: Weight(g87) = 1
    c: Equal(g87,g88)
    c: Equal(g87,g89)
    c: InternalAlignment(g87,g90)
    c: InternalAlignment(g88,g90)
    c: InternalAlignment(g89,g90)
    c: InternalAlignment(g91,g90)
    c: InternalAlignment(g92,g90)
    c: Block(g84)
    c: Block(g90)
    c: Coincident(g93,g84)
    c: Coincident(g93,g90)
    c: Vertical(g93)
    c: Coincident(g94,g84)
    c: Coincident(g94,g45)
    c: Coincident(g95,g45)
    c: Coincident(g95,g90)
    c: Weight(g96) = 1
    c: Equal(g96,g97)
    c: Equal(g96,g98)
    c: InternalAlignment(g96,g99)
    c: InternalAlignment(g97,g99)
    c: InternalAlignment(g98,g99)
    c: InternalAlignment(g100,g99)
    c: InternalAlignment(g101,g99)
    c: Weight(g102) = 1
    c: Equal(g102,g103)
    c: Equal(g102,g104)
    c: InternalAlignment(g102,g105)
    c: InternalAlignment(g103,g105)
    c: InternalAlignment(g104,g105)
    c: InternalAlignment(g106,g105)
    c: InternalAlignment(g107,g105)
    c: Block(g99)
    c: Block(g105)
    c: Coincident(g108,g99)
    c: Coincident(g108,g105)
    c: Vertical(g108)
    c: Coincident(g109,g105)
    c: Coincident(g109,g63)
    c: Coincident(g110,g63)
    c: Coincident(g110,g99)
    c: Weight(g111) = 1
    c: Equal(g111,g112)
    c: Equal(g111,g113)
    c: InternalAlignment(g111,g114)
    c: InternalAlignment(g112,g114)
    c: InternalAlignment(g113,g114)
    c: InternalAlignment(g115,g114)
    c: InternalAlignment(g116,g114)
    c: Weight(g117) = 1
    c: Equal(g117,g118)
    c: Equal(g117,g119)
    c: InternalAlignment(g117,g120)
    c: InternalAlignment(g118,g120)
    c: InternalAlignment(g119,g120)
    c: InternalAlignment(g121,g120)
    c: InternalAlignment(g122,g120)
    c: Block(g114)
    c: Block(g120)
    c: Coincident(g123,g114)
    c: Coincident(g123,g120)
    c: Vertical(g123)
    c: Coincident(g124,g120)
    c: Coincident(g124,g57)
    c: Coincident(g125,g57)
    c: Coincident(g125,g114)
    c: Weight(g126) = 1
    c: Equal(g126,g127)
    c: Equal(g126,g128)
    c: InternalAlignment(g126,g129)
    c: InternalAlignment(g127,g129)
    c: InternalAlignment(g128,g129)
    c: InternalAlignment(g130,g129)
    c: InternalAlignment(g131,g129)
    c: Weight(g132) = 1
    c: Equal(g132,g133)
    c: Equal(g132,g134)
    c: InternalAlignment(g132,g135)
    c: InternalAlignment(g133,g135)
    c: InternalAlignment(g134,g135)
    c: InternalAlignment(g136,g135)
    c: InternalAlignment(g137,g135)
    c: Weight(g138) = 1
    c: Equal(g138,g139)
    c: Equal(g138,g140)
    c: InternalAlignment(g138,g141)
    c: InternalAlignment(g139,g141)
    c: InternalAlignment(g140,g141)
    c: InternalAlignment(g142,g141)
    c: InternalAlignment(g143,g141)
    c: Weight(g144) = 1
    c: Equal(g144,g145)
    c: Equal(g144,g146)
    c: InternalAlignment(g144,g147)
    c: InternalAlignment(g145,g147)
    c: InternalAlignment(g146,g147)
    c: InternalAlignment(g148,g147)
    c: InternalAlignment(g149,g147)
    c: Block(g147)
    c: Block(g141)
    c: Block(g135)
    c: Block(g129)
    c: Coincident(g150,g25)
    c: Coincident(g150,g147)
    c: Coincident(g151,g147)
    c: Coincident(g151,g141)
    c: Horizontal(g151)
    c: Coincident(g152,g141)
    c: Coincident(g152,g25)
    c: Vertical(g152)
    c: Coincident(g153,g19)
    c: Coincident(g153,g135)
    c: Vertical(g153)
    c: Coincident(g154,g135)
    c: Coincident(g154,g129)
    c: Horizontal(g154)
    c: Coincident(g155,g129)
    c: Coincident(g155,g19)
    c: Weight(g156) = 1
    c: Equal(g156,g157)
    c: Equal(g156,g158)
    c: InternalAlignment(g156,g159)
    c: InternalAlignment(g157,g159)
    c: InternalAlignment(g158,g159)
    c: InternalAlignment(g160,g159)
    c: InternalAlignment(g161,g159)
    c: Weight(g162) = 1
    c: Equal(g162,g163)
    c: Equal(g162,g164)
    c: InternalAlignment(g162,g165)
    c: InternalAlignment(g163,g165)
    c: InternalAlignment(g164,g165)
    c: InternalAlignment(g166,g165)
    c: InternalAlignment(g167,g165)
    c: Weight(g168) = 1
    c: Equal(g168,g169)
    c: Equal(g168,g170)
    c: InternalAlignment(g168,g171)
    c: InternalAlignment(g169,g171)
    c: InternalAlignment(g170,g171)
    c: InternalAlignment(g172,g171)
    c: InternalAlignment(g173,g171)
    c: Weight(g174) = 1
    c: Equal(g174,g175)
    c: Equal(g174,g176)
    c: InternalAlignment(g174,g177)
    c: InternalAlignment(g175,g177)
    c: InternalAlignment(g176,g177)
    c: InternalAlignment(g178,g177)
    c: InternalAlignment(g179,g177)
    c: Block(g177)
    c: Block(g171)
    c: Block(g165)
    c: Block(g159)
    c: Coincident(g180,g177)
    c: Coincident(g180,g171)
    c: Horizontal(g180)
    c: Coincident(g181,g171)
    c: Coincident(g181,g7)
    c: Vertical(g181)
    c: Coincident(g182,g13)
    c: Coincident(g182,g165)
    c: Vertical(g182)
    c: Coincident(g183,g165)
    c: Coincident(g183,g159)
    c: Horizontal(g183)
    c: Coincident(g184,g159)
    c: Coincident(g184,g13)
    c: Coincident(g185,g7)
    c: Weight(g186) = 1
    c: Equal(g186,g187)
    c: Equal(g186,g188)
    c: InternalAlignment(g186,g189)
    c: InternalAlignment(g187,g189)
    c: InternalAlignment(g188,g189)
    c: InternalAlignment(g190,g189)
    c: InternalAlignment(g191,g189)
    c: Weight(g192) = 1
    c: Equal(g192,g193)
    c: Equal(g192,g194)
    c: InternalAlignment(g192,g195)
    c: InternalAlignment(g193,g195)
    c: InternalAlignment(g194,g195)
    c: InternalAlignment(g196,g195)
    c: InternalAlignment(g197,g195)
    c: Block(g195)
    c: Block(g189)
    c: Coincident(g198,g195)
    c: Coincident(g198,g31)
    c: Coincident(g199,g31)
    c: Coincident(g199,g189)
    c: Coincident(g200,g189)
    c: Coincident(g200,g195)
    c: Vertical(g200)
    c: Weight(g201) = 1
    c: Equal(g201,g202)
    c: Equal(g201,g203)
    c: InternalAlignment(g201,g204)
    c: InternalAlignment(g202,g204)
    c: InternalAlignment(g203,g204)
    c: InternalAlignment(g205,g204)
    c: InternalAlignment(g206,g204)
    c: Weight(g207) = 1
    c: Equal(g207,g208)
    c: Equal(g207,g209)
    c: InternalAlignment(g207,g210)
    c: InternalAlignment(g208,g210)
    c: InternalAlignment(g209,g210)
    c: InternalAlignment(g211,g210)
    c: InternalAlignment(g212,g210)
    c: Block(g210)
    c: Block(g204)
    c: Coincident(g213,g204)
    c: Coincident(g213,g37)
    c: Coincident(g214,g37)
    c: Coincident(g214,g210)
    c: Coincident(g215,g210)
    c: Coincident(g215,g204)
    c: Vertical(g215)
    c: Horizontal(g216)
    c: Block(g216)
    c: Vertical(g217)
    c: Block(g217)
    c: Block(g218)
    c: Weight(g219) = 1
    c: Equal(g219,g220)
    c: Equal(g219,g221)
    c: InternalAlignment(g219,g222)
    c: InternalAlignment(g220,g222)
    c: InternalAlignment(g221,g222)
    c: InternalAlignment(g223,g222)
    c: InternalAlignment(g224,g222)
    c: Weight(g225) = 1
    c: Equal(g225,g226)
    c: Equal(g225,g227)
    c: InternalAlignment(g225,g228)
    c: InternalAlignment(g226,g228)
    c: InternalAlignment(g227,g228)
    c: InternalAlignment(g229,g228)
    c: InternalAlignment(g230,g228)
    c: Weight(g231) = 1
    c: Equal(g231,g232)
    c: Equal(g231,g233)
    c: InternalAlignment(g231,g234)
    c: InternalAlignment(g232,g234)
    c: InternalAlignment(g233,g234)
    c: InternalAlignment(g235,g234)
    c: InternalAlignment(g236,g234)
    c: Weight(g237) = 1
    c: Equal(g237,g238)
    c: Equal(g237,g239)
    c: InternalAlignment(g237,g240)
    c: InternalAlignment(g238,g240)
    c: InternalAlignment(g239,g240)
    c: InternalAlignment(g241,g240)
    c: InternalAlignment(g242,g240)
    c: Block(g222)
    c: Block(g228)
    c: Block(g234)
    c: Block(g240)
    c: Coincident(g243,g228)
    c: Coincident(g243,g222)
    c: Horizontal(g243)
    c: Block(g185)
    c: Weight(g244) = 1
    c: Equal(g244,g245)
    c: Equal(g244,g246)
    c: InternalAlignment(g244,g247)
    c: InternalAlignment(g245,g247)
    c: InternalAlignment(g246,g247)
    c: InternalAlignment(g248,g247)
    c: InternalAlignment(g249,g247)
    c: Weight(g250) = 1
    c: Equal(g250,g251)
    c: Equal(g250,g252)
    c: InternalAlignment(g250,g253)
    c: InternalAlignment(g251,g253)
    c: InternalAlignment(g252,g253)
    c: InternalAlignment(g254,g253)
    c: InternalAlignment(g255,g253)
    c: Block(g247)
    c: Block(g253)
    c: Coincident(g256,g247)
    c: Coincident(g256,g253)
    c: Weight(g257) = 1
    c: Equal(g257,g258)
    c: Equal(g257,g259)
    c: InternalAlignment(g257,g260)
    c: InternalAlignment(g258,g260)
    c: InternalAlignment(g259,g260)
    c: InternalAlignment(g261,g260)
    c: InternalAlignment(g262,g260)
    c: Weight(g263) = 1
    c: Equal(g263,g264)
    c: Equal(g263,g265)
    c: InternalAlignment(g263,g266)
    c: InternalAlignment(g264,g266)
    c: InternalAlignment(g265,g266)
    c: InternalAlignment(g267,g266)
    c: InternalAlignment(g268,g266)
    c: Weight(g269) = 1
    c: Equal(g269,g270)
    c: Equal(g269,g271)
    c: InternalAlignment(g269,g272)
    c: InternalAlignment(g270,g272)
    c: InternalAlignment(g271,g272)
    c: InternalAlignment(g273,g272)
    c: InternalAlignment(g274,g272)
    c: Block(g272)
    c: Block(g266)
    c: Block(g260)
    c: Coincident(g275,g266)
    c: Coincident(g275,g260)
    c: Coincident(g276,g260)
    c: Coincident(g276,g272)
    c: Vertical(g276)
    c: Coincident(g277,g272)
    c: Coincident(g277,g266)
    c: Horizontal(g277)
    c: Weight(g278) = 1
    c: Equal(g278,g279)
    c: InternalAlignment(g278,g280)
    c: InternalAlignment(g279,g280)
    c: InternalAlignment(g281,g280)
    c: InternalAlignment(g282,g280)
    c: Weight(g283) = 1
    c: InternalAlignment(g284,g286)
    c: InternalAlignment(g285,g286)
    c: InternalAlignment(g287,g286)
    c: InternalAlignment(g288,g286)
    c: Weight(g289) = 1
    c: Equal(g289,g290)
    c: Equal(g289,g291)
    c: InternalAlignment(g289,g292)
    c: InternalAlignment(g290,g292)
    c: InternalAlignment(g291,g292)
    c: InternalAlignment(g293,g292)
    c: InternalAlignment(g294,g292)
    c: Equal(g295,g296)
    c: Equal(g295,g297)
    c: InternalAlignment(g295,g298)
    c: InternalAlignment(g296,g298)
    c: InternalAlignment(g297,g298)
    c: InternalAlignment(g299,g298)
    c: InternalAlignment(g300,g298)
    c: Block(g286)
    c: Block(g292)
    c: Block(g298)
    c: Block(g280)
    c: Coincident(g301,g280)
    c: Coincident(g301,g286)
    c: Horizontal(g301)
    c: Coincident(g302,g286)
    c: Coincident(g302,g292)
    c: Vertical(g302)
    c: Coincident(g303,g292)
    c: Coincident(g303,g298)
    c: Horizontal(g303)
    c: Coincident(g304,g298)
    c: Coincident(g304,g280)
    c: Weight(g305) = 1
    c: Equal(g305,g306)
    c: Equal(g305,g307)
    c: InternalAlignment(g305,g308)
    c: InternalAlignment(g306,g308)
    c: InternalAlignment(g307,g308)
    c: InternalAlignment(g309,g308)
    c: InternalAlignment(g310,g308)
    c: Weight(g311) = 1
    c: Equal(g311,g312)
    c: Equal(g311,g313)
    c: InternalAlignment(g311,g314)
    c: InternalAlignment(g312,g314)
    c: InternalAlignment(g313,g314)
    c: InternalAlignment(g315,g314)
    c: InternalAlignment(g316,g314)
    c: Weight(g317) = 1
    c: Equal(g317,g318)
    c: Equal(g317,g319)
    c: InternalAlignment(g317,g320)
    c: InternalAlignment(g318,g320)
    c: InternalAlignment(g319,g320)
    c: InternalAlignment(g321,g320)
    c: InternalAlignment(g322,g320)
    c: Block(g320)
    c: Block(g314)
    c: Block(g308)
    c: Coincident(g323,g320)
    c: Coincident(g323,g314)
    c: Horizontal(g323)
    c: Coincident(g324,g314)
    c: Coincident(g324,g308)
    c: Vertical(g324)
    c: Coincident(g325,g308)
    c: Coincident(g325,g320)
    c: InternalAlignment(g326,g327)
    c: InternalAlignment(g328,g327)
    c: InternalAlignment(g329,g327)
    c: Block(g327)
    c: Equal(g330,g331)
    c: Equal(g330,g332)
    c: InternalAlignment(g330,g333)
    c: InternalAlignment(g331,g333)
    c: InternalAlignment(g332,g333)
    c: InternalAlignment(g334,g333)
    c: InternalAlignment(g335,g333)
    c: Block(g333)
    c: Coincident(g336,g327)
    c: Horizontal(g336)
    c: Block(g336)
    c: Coincident(g337,g327)
    c: Coincident(g337,g253)
    c: Vertical(g337)
    c: Coincident(g338,g333)
    c: Coincident(g338,g247)
    c: Vertical(g338)
    c: Block(g339)
    c: Block(g2)
    c: Distance(g337) = 119.89
    c: Coincident(g340,g339)
    c: Coincident(g340,g2)
    c: Coincident(g341,g2)
    c: Coincident(g341,g339)
    c: Block(g3)
    c: Block(g342)
    c: Coincident(g343,g342)
    c: Coincident(g343,g3)
    c: Coincident(g344,g342)
    c: Coincident(g344,g3)
    c: Block(g344)
    c: Block(g343)
    c: Weight(g345) = 1
    c: Equal(g345,g346)
    c: Equal(g345,g347)
    c: InternalAlignment(g345,g348)
    c: InternalAlignment(g346,g348)
    c: InternalAlignment(g347,g348)
    c: InternalAlignment(g349,g348)
    c: InternalAlignment(g350,g348)
    c: Weight(g351) = 1
    c: Equal(g351,g352)
    c: Equal(g351,g353)
    c: InternalAlignment(g351,g354)
    c: InternalAlignment(g352,g354)
    c: InternalAlignment(g353,g354)
    c: InternalAlignment(g355,g354)
    c: InternalAlignment(g356,g354)
    c: Weight(g357) = 1
    c: Equal(g357,g358)
    c: Equal(g357,g359)
    c: InternalAlignment(g357,g360)
    c: InternalAlignment(g358,g360)
    c: InternalAlignment(g359,g360)
    c: InternalAlignment(g361,g360)
    c: InternalAlignment(g362,g360)
    c: Weight(g363) = 1
    c: Equal(g363,g364)
    c: Equal(g363,g365)
    c: InternalAlignment(g363,g366)
    c: InternalAlignment(g364,g366)
    c: InternalAlignment(g365,g366)
    c: InternalAlignment(g367,g366)
    c: InternalAlignment(g368,g366)
    c: Block(g366)
    c: Block(g360)
    c: Block(g354)
    c: Block(g348)
    c: Coincident(g369,g366)
    c: Coincident(g369,g348)
    c: Vertical(g369)
    c: Coincident(g370,g348)
    c: Coincident(g370,g354)
    c: Coincident(g371,g354)
    c: Coincident(g371,g360)
    c: Vertical(g371)
    c: Coincident(g372,g360)
    c: Coincident(g372,g366)
    c: Horizontal(g372)
FEATURE [Part::Extrusion] Extrude005
  Base = -> Sketch003
  Dir = (0,0,1)
  DirMode = 2
  FaceMakerClass = Part::FaceMakerBullseye
  LengthFwd = 24
  LengthRev = 0
  Solid = true
  Symmetric = false
